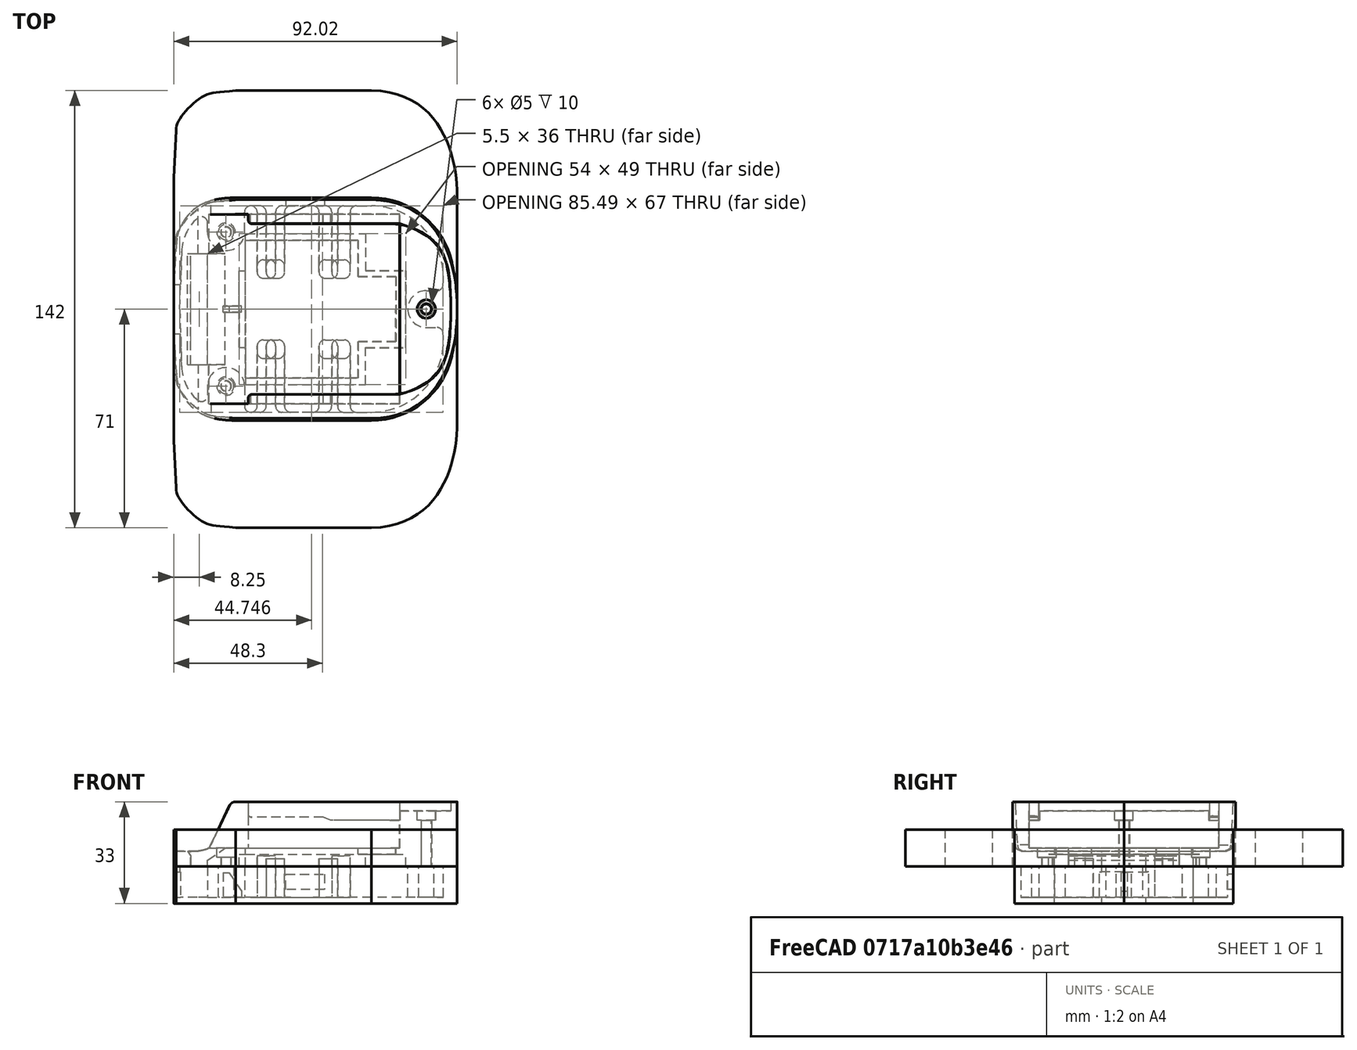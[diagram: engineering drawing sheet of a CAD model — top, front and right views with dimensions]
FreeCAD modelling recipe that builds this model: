
FCSTD DOCUMENT  (FreeCAD 1.0R39319 (Git))
Label: Makita LXT 18V - Battery Adapter v2
License: Creative Commons Attribution 4.0
LicenseURL: https://creativecommons.org/licenses/by/4.0/
objects: Sketcher::SketchObject×30, PartDesign::Pocket×23, TechDraw::DrawViewDimension×9, PartDesign::Pad×7, PartDesign::Body×5, TechDraw::DrawProjGroupItem×3, PartDesign::Mirrored×3, TechDraw::DrawSVGTemplate×2, TechDraw::DrawPage×2, Mesh::Feature×1, Part::Feature×1, TechDraw::DrawProjGroup×1
note: 180 computed .brp shape members not serialized (recipe doc carries the construction recipe); baked Part::Feature solids carry a one-line shape summary decoded from their .brp

FEATURE [Sketcher::SketchObject] Sketch
  ArcFitTolerance = 0
  AttachmentSupport = -> [XY_Plane]
  FullyConstrained = false
  MakeInternals = false
  MapMode = 5
  sketch-geometry (26):
    g0: ArcOfCircle CenterX=259.65 CenterY=-2.5774e-06 CenterZ=0 NormalX=0 NormalY=0 NormalZ=1 AngleXU=0 Radius=259.65 StartAngle=3.05831 EndAngle=3.14159
    g1: ArcOfCircle CenterX=16.3351 CenterY=20.3115 CenterZ=0 NormalX=0 NormalY=0 NormalZ=1 AngleXU=0 Radius=15.4888 StartAngle=1.76803 EndAngle=3.05831
    g2: LineSegment StartX=20 StartY=36.1629 StartZ=0 EndX=64.2 EndY=36.1629 EndZ=0
    g3: ArcOfCircle CenterX=64.2 CenterY=9.3939 CenterZ=0 NormalX=0 NormalY=0 NormalZ=1 AngleXU=0 Radius=26.769 StartAngle=0.218634 EndAngle=1.5708
    g4: ArcOfCircle CenterX=21.9206 CenterY=0 CenterZ=0 NormalX=0 NormalY=0 NormalZ=1 AngleXU=0 Radius=70.0794 StartAngle=0 EndAngle=0.218634
    g5: ArcOfCircle CenterX=20 CenterY=1.97116 CenterZ=0 NormalX=0 NormalY=0 NormalZ=1 AngleXU=0 Radius=34.1917 StartAngle=1.5708 EndAngle=1.76803
    g6: Circle CenterX=17 CenterY=25 CenterZ=0 NormalX=0 NormalY=0 NormalZ=1 AngleXU=0 Radius=1.6
    g7: ArcOfCircle CenterX=82 CenterY=0 CenterZ=0 NormalX=0 NormalY=0 NormalZ=1 AngleXU=0 Radius=1.6 StartAngle=0 EndAngle=3.14159
    g8: LineSegment StartX=23.3 StartY=0 StartZ=0 EndX=23.3 EndY=22.4 EndZ=0
    g9: LineSegment StartX=23.3 StartY=22.4 StartZ=0 EndX=59.9 EndY=22.4 EndZ=0
    g10: LineSegment StartX=59.9 StartY=22.4 StartZ=0 EndX=59.9 EndY=10.5 EndZ=0
    g11: LineSegment StartX=59.9 StartY=10.5 StartZ=0 EndX=72.1 EndY=10.5 EndZ=0
    g12: LineSegment StartX=72.1 StartY=10.5 StartZ=0 EndX=72.1 EndY=0 EndZ=0
    g13: ArcOfCircle CenterX=259.65 CenterY=2.5774e-06 CenterZ=0 NormalX=0 NormalY=0 NormalZ=1 AngleXU=0 Radius=259.65 StartAngle=3.14159 EndAngle=3.22488
    g14: ArcOfCircle CenterX=16.3351 CenterY=-20.3115 CenterZ=0 NormalX=0 NormalY=0 NormalZ=1 AngleXU=0 Radius=15.4888 StartAngle=3.22488 EndAngle=4.51516
    g15: LineSegment StartX=20 StartY=-36.1629 StartZ=0 EndX=64.2 EndY=-36.1629 EndZ=0
    g16: ArcOfCircle CenterX=64.2 CenterY=-9.3939 CenterZ=0 NormalX=0 NormalY=0 NormalZ=1 AngleXU=0 Radius=26.769 StartAngle=4.71239 EndAngle=6.06455
    g17: ArcOfCircle CenterX=21.9206 CenterY=0 CenterZ=0 NormalX=0 NormalY=0 NormalZ=1 AngleXU=0 Radius=70.0794 StartAngle=6.06455 EndAngle=6.28319
    g18: ArcOfCircle CenterX=20 CenterY=-1.97116 CenterZ=0 NormalX=0 NormalY=0 NormalZ=1 AngleXU=0 Radius=34.1917 StartAngle=4.51516 EndAngle=4.71239
    g19: Circle CenterX=17 CenterY=-25 CenterZ=0 NormalX=0 NormalY=0 NormalZ=1 AngleXU=0 Radius=1.6
    g20: ArcOfCircle CenterX=82 CenterY=0 CenterZ=0 NormalX=0 NormalY=0 NormalZ=1 AngleXU=0 Radius=1.6 StartAngle=3.14159 EndAngle=6.28319
    g21: LineSegment StartX=23.3 StartY=0 StartZ=0 EndX=23.3 EndY=-22.4 EndZ=0
    g22: LineSegment StartX=23.3 StartY=-22.4 StartZ=0 EndX=59.9 EndY=-22.4 EndZ=0
    g23: LineSegment StartX=59.9 StartY=-22.4 StartZ=0 EndX=59.9 EndY=-10.5 EndZ=0
    g24: LineSegment StartX=59.9 StartY=-10.5 StartZ=0 EndX=72.1 EndY=-10.5 EndZ=0
    g25: LineSegment StartX=72.1 StartY=-10.5 StartZ=0 EndX=72.1 EndY=0 EndZ=0
  constraints (64):
    c: Horizontal(g2)
    c: DistanceX(g2) = 20
    c: DistanceX(g2,g2) = 44.2
    c: Tangent(g4,g3) = -1.5708
    c: Tangent(g3,g2) = 1.5708
    c: Tangent(g1,g0) = -1.5708
    c: Tangent(g5,g2) = 1.5708
    c: Tangent(g5,g1) = -1.5708
    c: DistanceX(g0) = 0.9
    c: DistanceX(g1) = 13.3
    c: DistanceX(g4) = 92
    c: Coincident(g0,g-1)
    c: DistanceY(g0) = 21.6
    c: DistanceY(g1) = 35.5
    c: PointOnObject(g4,g-1)
    c: DistanceY(g3) = 15.2
    c: DistanceY(g6) = 25
    c: DistanceX(g6) = 17
    c: Diameter(g6) = 3.2
    c: PointOnObject(g7,g-1)
    c: PointOnObject(g7,g-1)
    c: PointOnObject(g7,g-1)
    c: DistanceX(g6,g7) = 65
    c: Equal(g7,g6)
    c: Tangent(g0,g-2)
    c: Perpendicular(g4,g-1)
    c: PointOnObject(g8,g-1)
    c: Vertical(g8)
    c: Coincident(g8,g9)
    c: Horizontal(g9)
    c: Coincident(g9,g10)
    c: Vertical(g10)
    c: Coincident(g10,g11)
    c: Horizontal(g11)
    c: Coincident(g11,g12)
    c: Vertical(g12)
    c: DistanceX(g8) = 23.3
    c: DistanceY(g8) = 22.4
    c: DistanceX(g9,g9) = 36.6
    c: DistanceY(g10,g10) = 11.9
    c: DistanceX(g11,g11) = 12.2
    c: PointOnObject(g12,g-1)
    c: Horizontal(g15)
    c: Tangent(g17,g16) = -1.5708
    c: Tangent(g16,g15) = -1.5708
    c: Tangent(g14,g13) = -1.5708
    c: Tangent(g18,g15) = -1.5708
    c: Tangent(g18,g14) = -1.5708
    c: Diameter(g19) = 3.2
    c: Equal(g20,g19)
    c: Vertical(g21)
    c: Coincident(g21,g22)
    c: Horizontal(g22)
    c: Coincident(g22,g23)
    c: Vertical(g23)
    c: Coincident(g23,g24)
    c: Horizontal(g24)
    c: Coincident(g24,g25)
    c: Vertical(g25)
    c: DistanceY(g15,g2) = 72.3257
    c: DistanceY(g19,g6) = 50
    c: DistanceX(g6,g7) = 66.6
    c: DistanceX(g6) = 17
    c: DistanceX(g4) = 92
FEATURE [Mesh::Feature] Makita_18V_Body  label="Makita 18V-Body"
  Placement = pos=(17,0,0) rot=(0,0,1;0rad)
FEATURE [PartDesign::Pad] Pad
  Direction = (0,0,1)
  Length = 21
  Length2 = 10
  Profile = -> Sketch
  ReferenceAxis = -> Sketch [N_Axis]
  Suppressed = false
  Type = 0
FEATURE [Sketcher::SketchObject] Sketch001
  ArcFitTolerance = 0
  AttachmentSupport = -> [XZ_Plane]
  FullyConstrained = true
  MakeInternals = false
  MapMode = 5
  Placement = pos=(0,0,0) rot=(1,0,0;1.5708rad)
  sketch-geometry (8):
    g0: LineSegment StartX=0 StartY=5 StartZ=0 EndX=0 EndY=21 EndZ=0
    g1: LineSegment StartX=0 StartY=21 StartZ=0 EndX=20 EndY=21 EndZ=0
    g2: LineSegment StartX=0 StartY=5 StartZ=0 EndX=7.9 EndY=5 EndZ=0
    g3: LineSegment StartX=18.2 StartY=19.8659 StartZ=0 EndX=11.9 EndY=6.7 EndZ=0
    g4: ArcOfCircle CenterX=20 CenterY=19.0045 CenterZ=0 NormalX=0 NormalY=0 NormalZ=1 AngleXU=0 Radius=1.99546 StartAngle=1.5708 EndAngle=2.69528
    g5: ArcOfCircle CenterX=10.0257 CenterY=7.59685 CenterZ=0 NormalX=0 NormalY=0 NormalZ=1 AngleXU=0 Radius=2.07779 StartAngle=4.99242 EndAngle=5.83688
    g6: ArcOfCircle CenterX=7.9 CenterY=5.60003 CenterZ=0 NormalX=0 NormalY=0 NormalZ=1 AngleXU=0 Radius=0.600034 StartAngle=4.71239 EndAngle=4.87983
    g7: ArcOfCircle CenterX=4.0509 CenterY=28.3729 CenterZ=0 NormalX=0 NormalY=0 NormalZ=1 AngleXU=0 Radius=23.6959 StartAngle=4.87983 EndAngle=4.99242
  constraints (22):
    c: PointOnObject(g0,g-2)
    c: PointOnObject(g0,g-2)
    c: Horizontal(g1)
    c: Coincident(g1,g0)
    c: DistanceY(g0) = 5
    c: DistanceY(g0) = 21
    c: Coincident(g2,g0)
    c: Horizontal(g2)
    c: Tangent(g4,g3) = -1.5708
    c: Tangent(g5,g3) = 1.5708
    c: Tangent(g4,g1) = 1.5708
    c: DistanceX(g1,g1) = 20
    c: DistanceX(g3) = 11.9
    c: DistanceY(g3) = 6.7
    c: DistanceX(g3) = 18.2
    c: Tangent(g6,g2) = -1.5708
    c: DistanceX(g2,g2) = 7.9
    c: Tangent(g7,g5) = -1.5708
    c: Tangent(g7,g6) = -1.5708
    c: DistanceX(g2,g6) = 0.1
    c: DistanceX(g5) = 10.6
    c: DistanceY(g5) = 5.6
FEATURE [PartDesign::Pocket] Pocket
  BaseFeature = -> Pad
  Direction = (0,1,-2e-16)
  Length = 5
  Length2 = 5
  Midplane = true
  Profile = -> Sketch001
  ReferenceAxis = -> Sketch001 [N_Axis]
  Suppressed = false
  Type = 1
FEATURE [Part::Feature] Makita_18V_Body001
  shape: bbox 92 x 71 x 21 mm, 5406 faces, 0 solids (baked)
FEATURE [Sketcher::SketchObject] Sketch002
  ArcFitTolerance = 0
  AttachmentSupport = -> [Pocket]
  FullyConstrained = false
  MakeInternals = false
  MapMode = 5
  Placement = pos=(0,0,21) rot=(0,0,1;0rad)
  sketch-geometry (16):
    g0: LineSegment StartX=24.2 StartY=30.78 StartZ=0 EndX=0 EndY=30.78 EndZ=0
    g1: LineSegment StartX=24.2 StartY=30.78 StartZ=0 EndX=24.2 EndY=28.88 EndZ=0
    g2: LineSegment StartX=25.4 StartY=27.68 StartZ=0 EndX=70.2 EndY=27.68 EndZ=0
    g3: ArcOfCircle CenterX=25.4 CenterY=28.88 CenterZ=0 NormalX=0 NormalY=0 NormalZ=1 AngleXU=0 Radius=1.2 StartAngle=3.14159 EndAngle=4.71239
    g4: ArcOfCircle CenterX=15.7361 CenterY=0 CenterZ=0 NormalX=0 NormalY=0 NormalZ=1 AngleXU=0 Radius=74.2639 StartAngle=0 EndAngle=0.199259
    g5: ArcOfCircle CenterX=74.666 CenterY=11.9002 CenterZ=0 NormalX=0 NormalY=0 NormalZ=1 AngleXU=0 Radius=14.1444 StartAngle=0.199259 EndAngle=0.868771
    g6: ArcOfCircle CenterX=70.2 CenterY=6.61972 CenterZ=0 NormalX=0 NormalY=0 NormalZ=1 AngleXU=0 Radius=21.0603 StartAngle=0.868771 EndAngle=1.5708
    g7: LineSegment StartX=0 StartY=0 StartZ=0 EndX=0 EndY=30.78 EndZ=0
    g8: LineSegment StartX=24.2 StartY=-30.78 StartZ=0 EndX=0 EndY=-30.78 EndZ=0
    g9: LineSegment StartX=24.2 StartY=-30.78 StartZ=0 EndX=24.2 EndY=-28.88 EndZ=0
    g10: LineSegment StartX=25.4 StartY=-27.68 StartZ=0 EndX=70.2 EndY=-27.68 EndZ=0
    g11: ArcOfCircle CenterX=25.4 CenterY=-28.88 CenterZ=0 NormalX=0 NormalY=0 NormalZ=1 AngleXU=0 Radius=1.2 StartAngle=1.5708 EndAngle=3.14159
    g12: ArcOfCircle CenterX=15.7361 CenterY=0 CenterZ=0 NormalX=0 NormalY=0 NormalZ=1 AngleXU=0 Radius=74.2639 StartAngle=6.08393 EndAngle=6.28319
    g13: ArcOfCircle CenterX=74.666 CenterY=-11.9002 CenterZ=0 NormalX=0 NormalY=0 NormalZ=1 AngleXU=0 Radius=14.1444 StartAngle=5.41441 EndAngle=6.08393
    g14: ArcOfCircle CenterX=70.2 CenterY=-6.61972 CenterZ=0 NormalX=0 NormalY=0 NormalZ=1 AngleXU=0 Radius=21.0603 StartAngle=4.71239 EndAngle=5.41441
    g15: LineSegment StartX=0 StartY=0 StartZ=0 EndX=0 EndY=-30.78 EndZ=0
  constraints (36):
    c: PointOnObject(g0,g-2)
    c: Horizontal(g0)
    c: DistanceY(g0) = 30.78
    c: DistanceX(g0,g0) = 24.2
    c: Coincident(g1,g0)
    c: Vertical(g1)
    c: Horizontal(g2)
    c: Tangent(g3,g1) = -1.5708
    c: Tangent(g3,g2) = -1.5708
    c: DistanceY(g1,g1) = 1.9
    c: Radius(g3) = 1.2
    c: PointOnObject(g4,g-1)
    c: Perpendicular(g4,g-1)
    c: DistanceX(g4) = 90
    c: DistanceY(g4) = 14.7
    c: Tangent(g6,g5) = -1.5708
    c: Tangent(g5,g4) = -1.5708
    c: Tangent(g6,g2) = 1.5708
    c: DistanceX(g2,g2) = 44.8
    c: DistanceX(g5) = 83.8
    c: DistanceY(g5) = 22.7
    c: PointOnObject(g7,g-1)
    c: Coincident(g7,g0)
    c: Vertical(g7)
    c: Horizontal(g8)
    c: Coincident(g9,g8)
    c: Vertical(g9)
    c: Horizontal(g10)
    c: Tangent(g11,g9) = 1.5708
    c: Tangent(g11,g10) = 1.5708
    c: Radius(g11) = 1.2
    c: Tangent(g14,g13) = -1.5708
    c: Tangent(g13,g12) = -1.5708
    c: Tangent(g14,g10) = -1.5708
    c: Coincident(g15,g8)
    c: Vertical(g15)
FEATURE [PartDesign::Pocket] Pocket001
  BaseFeature = -> Pocket
  Direction = (0,0,-1)
  Length = 3
  Length2 = 5
  Profile = -> Sketch002
  ReferenceAxis = -> Sketch002 [N_Axis]
  Suppressed = false
  Type = 0
FEATURE [Sketcher::SketchObject] Sketch003
  ArcFitTolerance = 0
  AttachmentSupport = -> [Pocket001]
  ExternalGeometry = -> [Sketch002]
  FullyConstrained = false
  MakeInternals = false
  MapMode = 5
  Placement = pos=(0,0,18) rot=(0,0,1;0rad)
  sketch-geometry (14):
    g0: LineSegment StartX=0 StartY=0 StartZ=0 EndX=0 EndY=30.78 EndZ=0
    g1: LineSegment StartX=0 StartY=30.78 StartZ=0 EndX=24.2 EndY=30.78 EndZ=0
    g2: LineSegment StartX=24.2 StartY=28.88 StartZ=0 EndX=24.2 EndY=30.78 EndZ=0
    g3: LineSegment StartX=25.4 StartY=27.68 StartZ=0 EndX=70.2 EndY=27.68 EndZ=0
    g4: ArcOfCircle CenterX=25.4 CenterY=28.88 CenterZ=0 NormalX=0 NormalY=0 NormalZ=1 AngleXU=0 Radius=1.2 StartAngle=3.14159 EndAngle=4.71239
    g5: LineSegment StartX=73.4 StartY=27.4355 StartZ=0 EndX=73.4 EndY=0 EndZ=0
    g6: ArcOfCircle CenterX=70.2 CenterY=6.61972 CenterZ=0 NormalX=0 NormalY=0 NormalZ=1 AngleXU=0 Radius=21.0603 StartAngle=1.41826 EndAngle=1.5708
    g7: LineSegment StartX=0 StartY=0 StartZ=0 EndX=0 EndY=-30.78 EndZ=0
    g8: LineSegment StartX=0 StartY=-30.78 StartZ=0 EndX=24.2 EndY=-30.78 EndZ=0
    g9: LineSegment StartX=24.2 StartY=-28.88 StartZ=0 EndX=24.2 EndY=-30.78 EndZ=0
    g10: LineSegment StartX=25.4 StartY=-27.68 StartZ=0 EndX=70.2 EndY=-27.68 EndZ=0
    g11: ArcOfCircle CenterX=25.4 CenterY=-28.88 CenterZ=0 NormalX=0 NormalY=0 NormalZ=1 AngleXU=0 Radius=1.2 StartAngle=1.5708 EndAngle=3.14159
    g12: LineSegment StartX=73.4 StartY=-27.4355 StartZ=0 EndX=73.4 EndY=0 EndZ=0
    g13: ArcOfCircle CenterX=70.2 CenterY=-6.61972 CenterZ=0 NormalX=0 NormalY=0 NormalZ=1 AngleXU=0 Radius=21.0603 StartAngle=4.71239 EndAngle=4.86492
  constraints (23):
    c: Coincident(g0,g-3)
    c: Coincident(g0,g-4)
    c: Coincident(g1,g0)
    c: Coincident(g1,g-4)
    c: Coincident(g2,g-7)
    c: Coincident(g2,g1)
    c: Coincident(g3,g-5)
    c: Coincident(g3,g-6)
    c: Coincident(g4,g2)
    c: Tangent(g4,g3) = -1.5708
    c: PointOnObject(g5,g-6)
    c: PointOnObject(g5,g-1)
    c: Vertical(g5)
    c: Coincident(g6,g5)
    c: Tangent(g6,g3) = 1.5708
    c: DistanceX(g5) = 73.4
    c: Coincident(g8,g7)
    c: Coincident(g9,g8)
    c: Coincident(g11,g9)
    c: Tangent(g11,g10) = 1.5708
    c: Vertical(g12)
    c: Coincident(g13,g12)
    c: Tangent(g13,g10) = -1.5708
FEATURE [PartDesign::Pocket] Pocket002
  BaseFeature = -> Pocket001
  Direction = (0,0,-1)
  Length = 12
  Length2 = 5
  Profile = -> Sketch003
  ReferenceAxis = -> Sketch003 [N_Axis]
  Suppressed = false
  Type = 0
FEATURE [Sketcher::SketchObject] Sketch004
  ArcFitTolerance = 0
  AttachmentSupport = -> [Pocket002]
  ExternalGeometry = -> [Pocket002]
  FullyConstrained = true
  MakeInternals = false
  MapMode = 5
  Placement = pos=(0,0,6) rot=(0,0,1;0rad)
  sketch-geometry (2):
    g0: Circle CenterX=17 CenterY=25 CenterZ=0 NormalX=0 NormalY=0 NormalZ=1 AngleXU=0 Radius=3
    g1: Circle CenterX=17 CenterY=-25 CenterZ=0 NormalX=0 NormalY=0 NormalZ=1 AngleXU=0 Radius=3
  constraints (4):
    c: Symmetric(g1,g0,g-1)
    c: Equal(g0,g1)
    c: Coincident(g-3,g0)
    c: Diameter(g0) = 6
FEATURE [PartDesign::Pocket] Pocket003
  BaseFeature = -> Pocket002
  Direction = (0,0,-1)
  Length = 3
  Length2 = 5
  Profile = -> Sketch004
  ReferenceAxis = -> Sketch004 [N_Axis]
  Suppressed = false
  Type = 0
FEATURE [Sketcher::SketchObject] Sketch005
  ArcFitTolerance = 0
  AttachmentSupport = -> [Pocket003]
  ExternalGeometry = -> [Pocket003]
  FullyConstrained = true
  MakeInternals = false
  MapMode = 5
  Placement = pos=(0,0,18) rot=(0,0,1;0rad)
  sketch-geometry (1):
    g0: Circle CenterX=82 CenterY=0 CenterZ=0 NormalX=0 NormalY=0 NormalZ=1 AngleXU=0 Radius=3
  constraints (2):
    c: Coincident(g0,g-3)
    c: Diameter(g0) = 6
FEATURE [PartDesign::Pocket] Pocket004
  BaseFeature = -> Pocket003
  Direction = (0,0,-1)
  Length = 3
  Length2 = 5
  Profile = -> Sketch005
  ReferenceAxis = -> Sketch005 [N_Axis]
  Suppressed = false
  Type = 0
FEATURE [Sketcher::SketchObject] Sketch006
  ArcFitTolerance = 0
  AttachmentSupport = -> [XZ_Plane]
  ExternalGeometry = -> [Sketch003]
  FullyConstrained = true
  MakeInternals = false
  MapMode = 5
  Placement = pos=(0,0,0) rot=(1,0,0;1.5708rad)
  sketch-geometry (7):
    g0: LineSegment StartX=73.4 StartY=15 StartZ=0 EndX=51 EndY=15 EndZ=0
    g1: LineSegment StartX=51 StartY=15 StartZ=0 EndX=48.5 EndY=16 EndZ=0
    g2: LineSegment StartX=48.5 StartY=16 StartZ=0 EndX=25 EndY=16 EndZ=0
    g3: LineSegment StartX=24.2 StartY=16.4 StartZ=0 EndX=25 EndY=16 EndZ=0
    g4: LineSegment StartX=24.2 StartY=16.4 StartZ=0 EndX=24.2 EndY=6 EndZ=0
    g5: LineSegment StartX=24.2 StartY=6 StartZ=0 EndX=73.4 EndY=6 EndZ=0
    g6: LineSegment StartX=73.4 StartY=6 StartZ=0 EndX=73.4 EndY=15 EndZ=0
  constraints (21):
    c: Horizontal(g0)
    c: Coincident(g1,g0)
    c: Coincident(g2,g1)
    c: Horizontal(g2)
    c: Coincident(g2,g3)
    c: Coincident(g4,g3)
    c: Vertical(g4)
    c: Coincident(g5,g4)
    c: Horizontal(g5)
    c: Coincident(g6,g5)
    c: Coincident(g6,g0)
    c: Vertical(g6)
    c: Vertical(g0,g-3)
    c: Vertical(g3,g-5)
    c: DistanceY(g4) = 6
    c: DistanceY(g4,g4) = 10.4
    c: DistanceY(g2) = 16
    c: DistanceX(g3,g2) = 0.8
    c: DistanceX(g2,g2) = 23.5
    c: DistanceY(g0) = 15
    c: DistanceX(g1,g0) = 2.5
FEATURE [PartDesign::Pocket] Pocket005
  BaseFeature = -> Pocket004
  Direction = (0,1,-2e-16)
  Length = 61.6
  Length2 = 5
  Midplane = true
  Profile = -> Sketch006
  ReferenceAxis = -> Sketch006 [N_Axis]
  Suppressed = false
  Type = 0
FEATURE [Sketcher::SketchObject] Sketch007
  ArcFitTolerance = 0
  AttachmentSupport = -> [Pocket005]
  ExternalGeometry = -> [Pocket005]
  FullyConstrained = false
  MakeInternals = false
  MapMode = 5
  Placement = pos=(0,0,0) rot=(1,0,0;3.14159rad)
  sketch-geometry (14):
    g0: LineSegment StartX=21.3 StartY=0 StartZ=0 EndX=21.3 EndY=12.5 EndZ=0
    g1: LineSegment StartX=21.3 StartY=12.5 StartZ=0 EndX=23.3 EndY=12.5 EndZ=0
    g2: LineSegment StartX=23.3 StartY=12.5 StartZ=0 EndX=23.3 EndY=24.5 EndZ=0
    g3: LineSegment StartX=23.3 StartY=24.5 StartZ=0 EndX=62.3 EndY=24.5 EndZ=0
    g4: LineSegment StartX=62.3 StartY=24.5 StartZ=0 EndX=62.3 EndY=12.5 EndZ=0
    g5: LineSegment StartX=62.3 StartY=12.5 StartZ=0 EndX=75.3 EndY=12.5 EndZ=0
    g6: LineSegment StartX=75.3 StartY=12.5 StartZ=0 EndX=75.3 EndY=0 EndZ=0
    g7: LineSegment StartX=21.3 StartY=0 StartZ=0 EndX=21.3 EndY=-12.5 EndZ=0
    g8: LineSegment StartX=21.3 StartY=-12.5 StartZ=0 EndX=23.3 EndY=-12.5 EndZ=0
    g9: LineSegment StartX=23.3 StartY=-12.5 StartZ=0 EndX=23.3 EndY=-24.5 EndZ=0
    g10: LineSegment StartX=23.3 StartY=-24.5 StartZ=0 EndX=62.3 EndY=-24.5 EndZ=0
    g11: LineSegment StartX=62.3 StartY=-24.5 StartZ=0 EndX=62.3 EndY=-12.5 EndZ=0
    g12: LineSegment StartX=62.3 StartY=-12.5 StartZ=0 EndX=75.3 EndY=-12.5 EndZ=0
    g13: LineSegment StartX=75.3 StartY=-12.5 StartZ=0 EndX=75.3 EndY=0 EndZ=0
  constraints (35):
    c: PointOnObject(g0,g-1)
    c: Vertical(g0)
    c: Coincident(g0,g1)
    c: PointOnObject(g1,g-3)
    c: Horizontal(g1)
    c: Coincident(g1,g2)
    c: Vertical(g2)
    c: Coincident(g2,g3)
    c: Horizontal(g3)
    c: Coincident(g3,g4)
    c: Vertical(g4)
    c: Coincident(g4,g5)
    c: Horizontal(g5)
    c: Coincident(g5,g6)
    c: PointOnObject(g6,g-1)
    c: Vertical(g6)
    c: DistanceY(g2) = 24.5
    c: DistanceY(g0,g0) = 12.5
    c: DistanceX(g1,g1) = 2
    c: DistanceX(g-4,g3) = 2.4
    c: DistanceY(g-5,g4) = 2
    c: DistanceX(g-5,g5) = 3.2
    c: Vertical(g7)
    c: Coincident(g7,g8)
    c: Horizontal(g8)
    c: Coincident(g8,g9)
    c: Vertical(g9)
    c: Coincident(g9,g10)
    c: Horizontal(g10)
    c: Coincident(g10,g11)
    c: Vertical(g11)
    c: Coincident(g11,g12)
    c: Horizontal(g12)
    c: Coincident(g12,g13)
    c: Vertical(g13)
FEATURE [PartDesign::Pocket] Pocket006
  BaseFeature = -> Pocket005
  Direction = (0,0,1)
  Length = 4
  Length2 = 5
  Profile = -> Sketch007
  ReferenceAxis = -> Sketch007 [N_Axis]
  Suppressed = false
  Type = 0
FEATURE [Sketcher::SketchObject] Sketch008
  ArcFitTolerance = 0
  AttachmentSupport = -> [XZ_Plane]
  FullyConstrained = true
  MakeInternals = false
  MapMode = 5
  Placement = pos=(0,0,0) rot=(1,0,0;1.5708rad)
  sketch-geometry (7):
    g0: LineSegment StartX=5.5 StartY=0 StartZ=0 EndX=11 EndY=0 EndZ=0
    g1: LineSegment StartX=11 StartY=0 StartZ=0 EndX=11 EndY=2 EndZ=0
    g2: LineSegment StartX=11 StartY=2 StartZ=0 EndX=16.7 EndY=6 EndZ=0
    g3: LineSegment StartX=16.7 StartY=6 StartZ=0 EndX=4.45 EndY=6 EndZ=0
    g4: LineSegment StartX=4.45 StartY=6 StartZ=0 EndX=4.45 EndY=5 EndZ=0
    g5: LineSegment StartX=4.45 StartY=5 StartZ=0 EndX=5.5 EndY=3.5 EndZ=0
    g6: LineSegment StartX=5.5 StartY=3.5 StartZ=0 EndX=5.5 EndY=0 EndZ=0
  constraints (21):
    c: PointOnObject(g0,g-1)
    c: PointOnObject(g0,g-1)
    c: Coincident(g0,g1)
    c: Vertical(g1)
    c: Coincident(g1,g2)
    c: Coincident(g2,g3)
    c: Horizontal(g3)
    c: Coincident(g3,g4)
    c: Vertical(g4)
    c: Coincident(g4,g5)
    c: Coincident(g5,g6)
    c: Coincident(g6,g0)
    c: Vertical(g6)
    c: DistanceX(g0) = 5.5
    c: DistanceX(g0) = 11
    c: DistanceY(g6,g6) = 3.5
    c: DistanceY(g1,g1) = 2
    c: DistanceY(g2) = 6
    c: DistanceX(g2) = 16.7
    c: DistanceY(g4) = 5
    c: DistanceX(g4) = 4.45
FEATURE [PartDesign::Pocket] Pocket007
  BaseFeature = -> Pocket006
  Direction = (0,1,-2e-16)
  Length = 36
  Length2 = 5
  Midplane = true
  Profile = -> Sketch008
  ReferenceAxis = -> Sketch008 [N_Axis]
  Suppressed = false
  Type = 0
FEATURE [PartDesign::Body] Body  label="Battery mount"
  AllowCompound = false
  Group = -> [Sketch,Pad,Sketch001,Pocket,Sketch002,Pocket001,Sketch003,Pocket002,Sketch004,Pocket003,Sketch005,Pocket004,Sketch006,Pocket005,Sketch007,Pocket006,Sketch008,Pocket007]
  Origin = -> Origin
  Tip = -> Pocket007
FEATURE [TechDraw::DrawSVGTemplate] Template
  EditableTexts = approval_person=B. Hecate; creator=Jon Sagebrand; date_of_issue=2026-02-17; document_type=Component Drawing; general_tolerances=ISO 2768-m; identification_number=DN; language_code=EN; legal_owner_1=Jonix; part_material=Stainless steel Mat.No. 1.4301; revision_index=AAA; scale=1 : 1; sheet_number=1 / 1; title=Makita LXT  - 18V - Battery holder
  Height = 210
  Orientation = 1
  Template = <path>
  Width = 297
FEATURE [TechDraw::DrawProjGroupItem] View
  CoarseView = false
  Direction = (0,0,-1)
  Focus = 100
  HardHidden = false
  IsoCount = 0
  IsoHidden = false
  IsoVisible = false
  LockPosition = false
  Perspective = false
  Rotation = 0
  RotationVector = (1,0,0)
  ScaleType = 0
  ScrubCount = 1
  SeamHidden = false
  SeamVisible = false
  SmoothHidden = false
  SmoothVisible = true
  Source = -> [Pocket007]
  Type = 0
  X = 157.417
  XDirection = (1,0,0)
  Y = 121.596
FEATURE [TechDraw::DrawViewDimension] Dimension
  AngleOverride = false
  Arbitrary = false
  ArbitraryTolerances = false
  BoxCorners = (2) [(-46,-36.1629,0),(46,36.1629,0)]
  EqualTolerance = true
  ExtensionAngle = 0
  FormatSpec = %.2w
  FormatSpecOverTolerance = %+.2w
  FormatSpecUnderTolerance = %+.2w
  Inverted = false
  LineAngle = 0
  LockPosition = false
  MeasureType = 1
  OverTolerance = 0
  References2D = -> [View]
  Rotation = 0
  ScaleType = 0
  TheoreticalExact = false
  Type = 2
  UnderTolerance = 0
  X = -60.9397
  Y = 3.59505
FEATURE [TechDraw::DrawViewDimension] Dimension001
  AngleOverride = false
  Arbitrary = false
  ArbitraryTolerances = false
  BoxCorners = (2) [(-46,-36.1629,0),(46,36.1629,0)]
  EqualTolerance = true
  ExtensionAngle = 0
  FormatSpec = %.2w
  FormatSpecOverTolerance = %+.2w
  FormatSpecUnderTolerance = %+.2w
  Inverted = false
  LineAngle = 0
  LockPosition = false
  MeasureType = 1
  OverTolerance = 0
  References2D = -> [View]
  Rotation = 0
  ScaleType = 0
  TheoreticalExact = false
  Type = 2
  UnderTolerance = 0
  X = -74.0234
  Y = 0
FEATURE [TechDraw::DrawViewDimension] Dimension002
  AngleOverride = false
  Arbitrary = false
  ArbitraryTolerances = false
  BoxCorners = (2) [(-46,-36.1629,0),(46,36.1629,0)]
  EqualTolerance = true
  ExtensionAngle = 0
  FormatSpec = %.2w
  FormatSpecOverTolerance = %+.2w
  FormatSpecUnderTolerance = %+.2w
  Inverted = false
  LineAngle = 0
  LockPosition = false
  MeasureType = 1
  OverTolerance = 0
  References2D = -> [View]
  Rotation = 0
  ScaleType = 0
  TheoreticalExact = false
  Type = 1
  UnderTolerance = 0
  X = 3.5
  Y = 57.7106
FEATURE [TechDraw::DrawViewDimension] Dimension003
  AngleOverride = false
  Arbitrary = false
  ArbitraryTolerances = false
  BoxCorners = (2) [(-46,-36.1629,0),(46,36.1629,0)]
  EqualTolerance = true
  ExtensionAngle = 0
  FormatSpec = %.2w
  FormatSpecOverTolerance = %+.2w
  FormatSpecUnderTolerance = %+.2w
  Inverted = false
  LineAngle = 0
  LockPosition = false
  MeasureType = 1
  OverTolerance = 0
  References2D = -> [View]
  Rotation = 0
  ScaleType = 0
  TheoreticalExact = false
  Type = 1
  UnderTolerance = 0
  X = 0
  Y = -48.6903
FEATURE [TechDraw::DrawViewDimension] Dimension004
  AngleOverride = false
  Arbitrary = false
  ArbitraryTolerances = false
  BoxCorners = (2) [(-46,-36.1629,0),(46,36.1629,0)]
  EqualTolerance = true
  ExtensionAngle = 0
  FormatSpec = %.2w
  FormatSpecOverTolerance = %+.2w
  FormatSpecUnderTolerance = %+.2w
  Inverted = false
  LineAngle = 0
  LockPosition = false
  MeasureType = 1
  OverTolerance = 0
  References2D = -> [View]
  Rotation = 0
  ScaleType = 0
  TheoreticalExact = false
  Type = 1
  UnderTolerance = 0
  X = -37.5
  Y = 57.7106
FEATURE [TechDraw::DrawViewDimension] Dimension005
  AngleOverride = false
  Arbitrary = false
  ArbitraryTolerances = false
  BoxCorners = (2) [(-46,-36.1629,0),(46,36.1629,0)]
  EqualTolerance = true
  ExtensionAngle = 0
  FormatSpec = %.2w
  FormatSpecOverTolerance = %+.2w
  FormatSpecUnderTolerance = %+.2w
  Inverted = false
  LineAngle = 0
  LockPosition = false
  MeasureType = 1
  OverTolerance = 0
  References2D = -> [View]
  Rotation = 0
  ScaleType = 0
  TheoreticalExact = false
  Type = 1
  UnderTolerance = 0
  X = 41
  Y = 57.7106
FEATURE [TechDraw::DrawPage] Page
  KeepUpdated = true
  NextBalloonIndex = 1
  ProjectionType = 0
  Template = -> Template
  Views = -> [View,Dimension,Dimension001,Dimension002,Dimension003,Dimension004,Dimension005]
FEATURE [Sketcher::SketchObject] Sketch009
  ArcFitTolerance = 1e-06
  AttachmentSupport = -> [XY_Plane001]
  FullyConstrained = false
  MakeInternals = false
  MapMode = 5
  sketch-geometry (35):
    g0: LineSegment StartX=23.3 StartY=22.3 StartZ=0 EndX=59.9 EndY=22.3 EndZ=0
    g1: LineSegment StartX=59.9 StartY=22.3 StartZ=0 EndX=59.9 EndY=10.55 EndZ=0
    g2: LineSegment StartX=59.9 StartY=10.55 StartZ=0 EndX=72.15 EndY=10.55 EndZ=0
    g3: LineSegment StartX=72.15 StartY=10.55 StartZ=0 EndX=72.15 EndY=0 EndZ=0
    g4: LineSegment StartX=72.15 StartY=0 StartZ=0 EndX=80.25 EndY=2e-16 EndZ=0
    g5: LineSegment StartX=83.75 StartY=0 StartZ=0 EndX=92 EndY=0 EndZ=0
    g6: ArcOfCircle CenterX=82 CenterY=0 CenterZ=0 NormalX=0 NormalY=0 NormalZ=1 AngleXU=0 Radius=1.75 StartAngle=0 EndAngle=3.14159
    g7: LineSegment StartX=0 StartY=6.35e-14 StartZ=0 EndX=5.5 EndY=0 EndZ=0
    g8: LineSegment StartX=5.5 StartY=0 StartZ=0 EndX=5.5 EndY=18 EndZ=0
    g9: LineSegment StartX=5.5 StartY=18 StartZ=0 EndX=11 EndY=18 EndZ=0
    g10: LineSegment StartX=11 StartY=0 StartZ=0 EndX=23.3 EndY=0 EndZ=0
    g11: LineSegment StartX=0.05 StartY=7.2 StartZ=0 EndX=0.75 EndY=22.55 EndZ=0
    g12: ArcOfCircle CenterX=518.425 CenterY=0 CenterZ=0 NormalX=0 NormalY=0 NormalZ=1 AngleXU=0 Radius=518.425 StartAngle=3.1277 EndAngle=3.14159
    g13: LineSegment StartX=11 StartY=0 StartZ=0 EndX=11 EndY=18 EndZ=0
    g14: LineSegment StartX=20.1 StartY=35.5 StartZ=0 EndX=64.2 EndY=35.5 EndZ=0
    g15-g20: Circle [constr] x6 (B-spline internal-alignment scaffolding for g21; pole/knot coordinates omitted)
    g21: BSplineCurve PolesCount=6 KnotsCount=4 Degree=3 IsPeriodic=0
    g22-g25: GeomPoint [constr] x4 (B-spline internal-alignment scaffolding for g21; pole/knot coordinates omitted)
    g26-g29: Circle [constr] x4 (B-spline internal-alignment scaffolding for g30; pole/knot coordinates omitted)
    g30: BSplineCurve PolesCount=4 KnotsCount=2 Degree=3 IsPeriodic=0
    g31: GeomPoint [constr] X=92 Y=0 Z=0
    g32: GeomPoint [constr] X=64.2 Y=35.5 Z=0
    g33: Circle CenterX=17 CenterY=25 CenterZ=0 NormalX=0 NormalY=0 NormalZ=1 AngleXU=0 Radius=1.75
    g34: LineSegment StartX=23.3 StartY=0 StartZ=0 EndX=23.3 EndY=22.3 EndZ=0
  constraints (71):
    c: PointOnObject(g10,g-1)
    c: Horizontal(g0)
    c: Coincident(g0,g1)
    c: Vertical(g1)
    c: Coincident(g1,g2)
    c: Horizontal(g2)
    c: Coincident(g2,g3)
    c: PointOnObject(g3,g-1)
    c: Vertical(g3)
    c: Coincident(g4,g3)
    c: PointOnObject(g4,g-1)
    c: PointOnObject(g5,g-1)
    c: PointOnObject(g5,g-1)
    c: Coincident(g6,g4)
    c: Coincident(g6,g5)
    c: PointOnObject(g6,g-1)
    c: Coincident(g7,g-1)
    c: PointOnObject(g7,g-1)
    c: Coincident(g8,g7)
    c: Vertical(g8)
    c: Horizontal(g9)
    c: PointOnObject(g10,g-1)
    c: DistanceX(g7,g7) = 5.5
    c: DistanceX(g7,g10) = 5.5
    c: Coincident(g9,g8)
    c: DistanceY(g8,g8) = 18
    c: Diameter(g6) = 3.5
    c: DistanceX(g5,g5) = 8.25
    c: DistanceX(g5) = 92
    c: DistanceX(g11) = 0.75
    c: DistanceY(g11) = 22.55
    c: Coincident(g12,g7)
    c: Coincident(g12,g11)
    c: DistanceX(g11) = 0.05
    c: DistanceY(g11) = 7.2
    c: Perpendicular(g12,g-1)
    c: Radius(g12) = 518.425
    c: Coincident(g13,g10)
    c: Coincident(g13,g9)
    c: Vertical(g13)
    c: Horizontal(g14)
    c: DistanceY(g14) = 35.5
    c: DistanceX(g14) = 20.1
    c: DistanceX(g14,g14) = 44.1
    c: Weight(g15) = 1
    c: Equal(g15, g16-g20) x5
    c: InternalAlignment(g15-g20 -> g21) x6
    c: InternalAlignment(g22-g25 -> g21) x4
    c: Coincident(g15,g11)
    c: Coincident(g20,g14)
    c: Weight(g26) = 1
    c: Equal(g26,g27)
    c: Equal(g26,g28)
    c: Equal(g26,g29)
    c: InternalAlignment(g26-g29 -> g30) x4
    c: InternalAlignment(g31,g30)
    c: InternalAlignment(g32,g30)
    c: Coincident(g26,g5)
    c: Coincident(g29,g14)
    c: DistanceY(g33) = 25
    c: DistanceX(g33,g6) = 65
    c: Equal(g33,g6)
    c: Coincident(g34,g10)
    c: Coincident(g34,g0)
    c: Vertical(g34)
    c: DistanceX(g10,g10) = 12.3
    c: DistanceY(g34,g34) = 22.3
    c: DistanceX(g0,g0) = 36.6
    c: DistanceY(g1,g1) = 11.75
    c: DistanceX(g2,g2) = 12.25
    c: DistanceX(g4,g4) = 8.1
FEATURE [PartDesign::Pad] Pad001
  Direction = (0,0,1)
  Length = 21
  Length2 = 10
  Profile = -> Sketch009
  ReferenceAxis = -> Sketch009 [N_Axis]
  Refine = true
  Suppressed = false
  Type = 0
FEATURE [Sketcher::SketchObject] Sketch010
  ArcFitTolerance = 1e-06
  AttachmentSupport = -> [Pad001]
  ExternalGeometry = -> [Pad001]
  FullyConstrained = false
  MakeInternals = false
  MapMode = 5
  Placement = pos=(0,0,0) rot=(1,0,0;1.5708rad)
  sketch-geometry (14):
    g0: LineSegment StartX=7.9 StartY=5 StartZ=0 EndX=0 EndY=5 EndZ=0
    g1: LineSegment StartX=0 StartY=5 StartZ=0 EndX=0 EndY=21 EndZ=0
    g2: LineSegment StartX=0 StartY=21 StartZ=0 EndX=20.05 EndY=21 EndZ=0
    g3: LineSegment StartX=18.1059 StartY=19.7681 StartZ=0 EndX=12.1 EndY=7.05 EndZ=0
    g4: ArcOfCircle CenterX=20.05 CenterY=18.85 CenterZ=0 NormalX=0 NormalY=0 NormalZ=1 AngleXU=0 Radius=2.15 StartAngle=1.5708 EndAngle=2.70041
    g5-g9: Circle [constr] x5 (B-spline internal-alignment scaffolding for g10; pole/knot coordinates omitted)
    g10: BSplineCurve PolesCount=5 KnotsCount=3 Degree=3 IsPeriodic=0
    g11: GeomPoint [constr] X=12.1 Y=7.05 Z=0
    g12: GeomPoint [constr] X=11.1765 Y=5.88818 Z=0
    g13: GeomPoint [constr] X=7.9 Y=5 Z=0
  constraints (23):
    c: PointOnObject(g0,g-2)
    c: Horizontal(g0)
    c: Coincident(g0,g1)
    c: Coincident(g1,g-3)
    c: Coincident(g1,g2)
    c: Horizontal(g2)
    c: DistanceY(g0) = 5
    c: DistanceX(g0,g0) = 7.9
    c: DistanceX(g2,g2) = 20.05
    c: DistanceX(g3) = 12.1
    c: DistanceY(g0,g3) = 2.05
    c: Coincident(g4,g3)
    c: Tangent(g4,g2) = 1.5708
    c: Tangent(g3,g4,g3) = -1.5708
    c: Radius(g4) = 2.15
    c: Weight(g5) = 1
    c: Equal(g5, g6-g9) x4
    c: InternalAlignment(g5-g9 -> g10) x5
    c: InternalAlignment(g11,g10)
    c: InternalAlignment(g12,g10)
    c: InternalAlignment(g13,g10)
    c: Coincident(g5,g3)
    c: Coincident(g9,g0)
FEATURE [PartDesign::Pocket] Pocket008
  BaseFeature = -> Pad001
  Direction = (0,1,-2e-16)
  Length = 5
  Length2 = 5
  Profile = -> Sketch010
  ReferenceAxis = -> Sketch010 [N_Axis]
  Refine = true
  Suppressed = false
  Type = 1
FEATURE [Sketcher::SketchObject] Sketch011
  ArcFitTolerance = 1e-06
  AttachmentSupport = -> [Pocket008]
  ExternalGeometry = -> [Pocket008]
  FullyConstrained = true
  MakeInternals = false
  MapMode = 5
  Placement = pos=(0,0,21) rot=(0,0,1;0rad)
  sketch-geometry (13):
    g0: LineSegment StartX=11 StartY=30.8 StartZ=0 EndX=11 EndY=0 EndZ=0
    g1: LineSegment StartX=11 StartY=0 StartZ=0 EndX=23.3 EndY=0 EndZ=0
    g2: LineSegment StartX=23.3 StartY=0 StartZ=0 EndX=23.3 EndY=22.3 EndZ=0
    g3: LineSegment StartX=23.3 StartY=22.3 StartZ=0 EndX=59.9 EndY=22.3 EndZ=0
    g4: LineSegment StartX=59.9 StartY=22.3 StartZ=0 EndX=59.9 EndY=10.55 EndZ=0
    g5: LineSegment StartX=59.9 StartY=10.55 StartZ=0 EndX=72.15 EndY=10.55 EndZ=0
    g6: LineSegment StartX=72.15 StartY=10.55 StartZ=0 EndX=72.15 EndY=0 EndZ=0
    g7: LineSegment StartX=72.15 StartY=0 StartZ=0 EndX=73.35 EndY=0 EndZ=0
    g8: LineSegment StartX=73.35 StartY=27.75 StartZ=0 EndX=25.4 EndY=27.75 EndZ=0
    g9: LineSegment StartX=24.2 StartY=28.95 StartZ=0 EndX=24.2 EndY=30.8 EndZ=0
    g10: LineSegment StartX=24.2 StartY=30.8 StartZ=0 EndX=11 EndY=30.8 EndZ=0
    g11: ArcOfCircle CenterX=25.4 CenterY=28.95 CenterZ=0 NormalX=0 NormalY=0 NormalZ=1 AngleXU=0 Radius=1.2 StartAngle=3.14159 EndAngle=4.71239
    g12: LineSegment StartX=73.35 StartY=27.75 StartZ=0 EndX=73.35 EndY=0 EndZ=0
  constraints (33):
    c: Vertical(g0)
    c: Coincident(g0,g1)
    c: PointOnObject(g1,g-1)
    c: Coincident(g1,g2)
    c: Coincident(g2,g-4)
    c: Vertical(g2)
    c: Coincident(g2,g3)
    c: Coincident(g3,g-4)
    c: Coincident(g3,g4)
    c: Coincident(g4,g-3)
    c: Coincident(g4,g5)
    c: Coincident(g5,g-3)
    c: Coincident(g5,g6)
    c: PointOnObject(g6,g-1)
    c: Vertical(g6)
    c: Coincident(g6,g7)
    c: PointOnObject(g7,g-1)
    c: Horizontal(g8)
    c: Vertical(g9)
    c: Coincident(g9,g10)
    c: Coincident(g10,g0)
    c: Horizontal(g10)
    c: Tangent(g11,g8) = 1.5708
    c: Tangent(g11,g9) = 1.5708
    c: DistanceY(g0) = 30.8
    c: DistanceX(g9) = 24.2
    c: DistanceY(g8) = 27.75
    c: Radius(g11) = 1.2
    c: DistanceX(g8,g8) = 47.95
    c: Coincident(g12,g8)
    c: Coincident(g12,g7)
    c: Vertical(g12)
    c: Coincident(g0,g-5)
FEATURE [PartDesign::Pocket] Pocket009
  BaseFeature = -> Pocket008
  Direction = (0,0,-1)
  Length = 15
  Length2 = 5
  Profile = -> Sketch011
  ReferenceAxis = -> Sketch011 [N_Axis]
  Refine = true
  Suppressed = false
  Type = 0
FEATURE [Sketcher::SketchObject] Sketch012
  ArcFitTolerance = 1e-06
  AttachmentSupport = -> [Pocket009]
  ExternalGeometry = -> [Pocket009]
  FullyConstrained = true
  MakeInternals = false
  MapMode = 5
  Placement = pos=(0,0,0) rot=(1,0,0;1.5708rad)
  sketch-geometry (3):
    g0: LineSegment StartX=16.7 StartY=6 StartZ=0 EndX=11 EndY=6 EndZ=0
    g1: LineSegment StartX=11 StartY=6 StartZ=0 EndX=11 EndY=2 EndZ=0
    g2: LineSegment StartX=11 StartY=2 StartZ=0 EndX=16.7 EndY=6 EndZ=0
  constraints (9):
    c: PointOnObject(g0,g-3)
    c: Horizontal(g0)
    c: Coincident(g0,g1)
    c: PointOnObject(g1,g-4)
    c: Coincident(g1,g2)
    c: Coincident(g2,g0)
    c: Vertical(g1)
    c: DistanceX(g0,g0) = 5.7
    c: DistanceY(g1,g1) = 4
FEATURE [PartDesign::Pocket] Pocket010
  BaseFeature = -> Pocket009
  Direction = (0,1,-2e-16)
  Length = 0
  Length2 = 5
  Profile = -> Sketch012
  ReferenceAxis = -> Sketch012 [N_Axis]
  Refine = true
  Suppressed = false
  Type = 3
  UpToFace = -> Pocket009 [Face21]
FEATURE [Sketcher::SketchObject] Sketch013
  ArcFitTolerance = 1e-06
  AttachmentSupport = -> [Pocket010]
  ExternalGeometry = -> [Pocket010]
  FullyConstrained = true
  MakeInternals = false
  MapMode = 5
  Placement = pos=(0,0,0) rot=(1,0,0;3.14159rad)
  sketch-geometry (14):
    g0: LineSegment StartX=72.15 StartY=-10.55 StartZ=0 EndX=59.9 EndY=-10.55 EndZ=0
    g1: LineSegment StartX=59.9 StartY=-10.55 StartZ=0 EndX=59.9 EndY=-22.3 EndZ=0
    g2: LineSegment StartX=59.9 StartY=-22.3 StartZ=0 EndX=23.3 EndY=-22.3 EndZ=0
    g3: LineSegment StartX=23.3 StartY=-22.3 StartZ=0 EndX=23.3 EndY=-24.5 EndZ=0
    g4: LineSegment StartX=23.3 StartY=-24.5 StartZ=0 EndX=62.3 EndY=-24.5 EndZ=0
    g5: LineSegment StartX=62.3 StartY=-24.5 StartZ=0 EndX=62.3 EndY=-12.55 EndZ=0
    g6: LineSegment StartX=62.3 StartY=-12.55 StartZ=0 EndX=75.35 EndY=-12.55 EndZ=0
    g7: LineSegment StartX=75.35 StartY=-12.55 StartZ=0 EndX=75.35 EndY=0 EndZ=0
    g8: LineSegment StartX=75.35 StartY=0 StartZ=0 EndX=72.15 EndY=0 EndZ=0
    g9: LineSegment StartX=72.15 StartY=0 StartZ=0 EndX=72.15 EndY=-10.55 EndZ=0
    g10: LineSegment StartX=23.3 StartY=0 StartZ=0 EndX=21.3 EndY=0 EndZ=0
    g11: LineSegment StartX=21.3 StartY=0 StartZ=0 EndX=21.3 EndY=-12.5 EndZ=0
    g12: LineSegment StartX=21.3 StartY=-12.5 StartZ=0 EndX=23.3 EndY=-12.5 EndZ=0
    g13: LineSegment StartX=23.3 StartY=-12.5 StartZ=0 EndX=23.3 EndY=0 EndZ=0
  constraints (38):
    c: Coincident(g-3,g0)
    c: Coincident(g0,g-3)
    c: Coincident(g0,g1)
    c: Coincident(g1,g-4)
    c: Coincident(g1,g2)
    c: Coincident(g2,g-4)
    c: Coincident(g2,g3)
    c: Coincident(g3,g4)
    c: Horizontal(g4)
    c: Coincident(g4,g5)
    c: Vertical(g5)
    c: Coincident(g5,g6)
    c: Horizontal(g6)
    c: Coincident(g6,g7)
    c: PointOnObject(g7,g-1)
    c: Vertical(g7)
    c: Coincident(g7,g8)
    c: PointOnObject(g8,g-1)
    c: Coincident(g8,g9)
    c: Coincident(g9,g0)
    c: Vertical(g9)
    c: Vertical(g3)
    c: Coincident(g10,g11)
    c: Coincident(g11,g12)
    c: Coincident(g12,g13)
    c: Coincident(g13,g10)
    c: Horizontal(g10)
    c: Horizontal(g12)
    c: Vertical(g11)
    c: Vertical(g13)
    c: PointOnObject(g10,g-1)
    c: Vertical(g12,g2)
    c: DistanceY(g13,g13) = 12.5
    c: DistanceX(g10,g10) = 2
    c: DistanceY(g3,g3) = 2.2
    c: DistanceX(g0,g5) = 2.4
    c: DistanceX(g8,g8) = 3.2
    c: DistanceY(g5,g0) = 2
FEATURE [PartDesign::Pocket] Pocket011
  BaseFeature = -> Pocket010
  Direction = (0,0,1)
  Length = 4
  Length2 = 5
  Profile = -> Sketch013
  ReferenceAxis = -> Sketch013 [N_Axis]
  Refine = true
  Suppressed = false
  Type = 0
FEATURE [Sketcher::SketchObject] Sketch014
  ArcFitTolerance = 1e-06
  AttachmentSupport = -> [Pocket011]
  ExternalGeometry = -> [Pocket011]
  FullyConstrained = false
  MakeInternals = false
  MapMode = 5
  Placement = pos=(0,0,21) rot=(0,0,1;0rad)
  sketch-geometry (9):
    g0: LineSegment StartX=73.35 StartY=27.75 StartZ=0 EndX=73.35 EndY=0 EndZ=0
    g1: LineSegment StartX=73.35 StartY=0 StartZ=0 EndX=89.95 EndY=0 EndZ=0
    g2-g5: Circle [constr] x4 (B-spline internal-alignment scaffolding for g6; pole/knot coordinates omitted)
    g6: BSplineCurve PolesCount=4 KnotsCount=2 Degree=3 IsPeriodic=0
    g7: GeomPoint [constr] X=89.95 Y=0 Z=0
    g8: GeomPoint [constr] X=73.35 Y=27.75 Z=0
  constraints (14):
    c: Coincident(g-3,g0)
    c: Coincident(g0,g-3)
    c: Coincident(g0,g1)
    c: PointOnObject(g1,g-1)
    c: DistanceX(g1,g1) = 16.6
    c: Weight(g2) = 1
    c: Equal(g2,g3)
    c: Equal(g2,g4)
    c: Equal(g2,g5)
    c: InternalAlignment(g2-g5 -> g6) x4
    c: InternalAlignment(g7,g6)
    c: InternalAlignment(g8,g6)
    c: Coincident(g2,g1)
    c: Coincident(g5,g0)
FEATURE [PartDesign::Pocket] Pocket012
  BaseFeature = -> Pocket011
  Direction = (0,0,-1)
  Length = 3
  Length2 = 5
  Profile = -> Sketch014
  ReferenceAxis = -> Sketch014 [N_Axis]
  Refine = true
  Suppressed = false
  Type = 0
FEATURE [Sketcher::SketchObject] Sketch015
  ArcFitTolerance = 1e-06
  AttachmentSupport = -> [Pocket012]
  ExternalGeometry = -> [Pocket012]
  FullyConstrained = true
  MakeInternals = false
  MapMode = 5
  Placement = pos=(0,27.75,0) rot=(1,0,0;1.5708rad)
  sketch-geometry (7):
    g0: LineSegment StartX=24.2 StartY=6 StartZ=0 EndX=73.35 EndY=6 EndZ=0
    g1: LineSegment StartX=73.35 StartY=6 StartZ=0 EndX=73.35 EndY=15 EndZ=0
    g2: LineSegment StartX=73.35 StartY=15 StartZ=0 EndX=51 EndY=15 EndZ=0
    g3: LineSegment StartX=51 StartY=15 StartZ=0 EndX=48.45 EndY=16 EndZ=0
    g4: LineSegment StartX=48.45 StartY=16 StartZ=0 EndX=25 EndY=16 EndZ=0
    g5: LineSegment StartX=25 StartY=16 StartZ=0 EndX=24.2 EndY=16.4 EndZ=0
    g6: LineSegment StartX=24.2 StartY=16.4 StartZ=0 EndX=24.2 EndY=6 EndZ=0
  constraints (19):
    c: Coincident(g-3,g0)
    c: Coincident(g0,g-4)
    c: Coincident(g0,g1)
    c: PointOnObject(g1,g-4)
    c: Coincident(g1,g2)
    c: Horizontal(g2)
    c: Coincident(g2,g3)
    c: Coincident(g3,g4)
    c: Horizontal(g4)
    c: Coincident(g4,g5)
    c: PointOnObject(g5,g-3)
    c: Coincident(g5,g6)
    c: Coincident(g6,g0)
    c: DistanceY(g6,g6) = 10.4
    c: DistanceY(g4) = 16
    c: DistanceX(g5,g4) = 0.8
    c: DistanceX(g4,g4) = 23.45
    c: DistanceY(g2) = 15
    c: DistanceX(g2,g2) = 22.35
FEATURE [PartDesign::Pocket] Pocket013
  BaseFeature = -> Pocket012
  Direction = (0,1,-2e-16)
  Length = 0
  Length2 = 5
  Profile = -> Sketch015
  ReferenceAxis = -> Sketch015 [N_Axis]
  Refine = true
  Suppressed = false
  Type = 3
  UpToFace = -> Pocket012 [Face35]
FEATURE [Sketcher::SketchObject] Sketch016
  ArcFitTolerance = 1e-06
  AttachmentSupport = -> [XY_Plane002]
  FullyConstrained = false
  MakeInternals = false
  MapMode = 5
  sketch-geometry (36):
    g0: LineSegment [constr] StartX=23.3 StartY=22.3 StartZ=0 EndX=59.9 EndY=22.3 EndZ=0
    g1: LineSegment [constr] StartX=59.9 StartY=22.3 StartZ=0 EndX=59.9 EndY=10.55 EndZ=0
    g2: LineSegment [constr] StartX=59.9 StartY=10.55 StartZ=0 EndX=72.15 EndY=10.55 EndZ=0
    g3: LineSegment [constr] StartX=72.15 StartY=10.55 StartZ=0 EndX=72.15 EndY=0 EndZ=0
    g4: LineSegment [constr] StartX=72.15 StartY=0 StartZ=0 EndX=80.25 EndY=2e-16 EndZ=0
    g5: LineSegment [constr] StartX=83.75 StartY=0 StartZ=0 EndX=92 EndY=0 EndZ=0
    g6: ArcOfCircle [constr] CenterX=82 CenterY=0 CenterZ=0 NormalX=0 NormalY=0 NormalZ=1 AngleXU=0 Radius=1.75 StartAngle=0 EndAngle=3.14159
    g7: LineSegment [constr] StartX=0 StartY=6.35e-14 StartZ=0 EndX=5.5 EndY=0 EndZ=0
    g8: LineSegment [constr] StartX=5.5 StartY=0 StartZ=0 EndX=5.5 EndY=18 EndZ=0
    g9: LineSegment [constr] StartX=5.5 StartY=18 StartZ=0 EndX=11 EndY=18 EndZ=0
    g10: LineSegment [constr] StartX=11 StartY=0 StartZ=0 EndX=23.3 EndY=0 EndZ=0
    g11: LineSegment StartX=0.05 StartY=7.2 StartZ=0 EndX=0.75 EndY=22.55 EndZ=0
    g12: ArcOfCircle CenterX=518.425 CenterY=0 CenterZ=0 NormalX=0 NormalY=0 NormalZ=1 AngleXU=0 Radius=518.425 StartAngle=3.1277 EndAngle=3.14159
    g13: LineSegment [constr] StartX=11 StartY=0 StartZ=0 EndX=11 EndY=18 EndZ=0
    g14: LineSegment StartX=20.1 StartY=35.5 StartZ=0 EndX=64.2 EndY=35.5 EndZ=0
    g15-g20: Circle [constr] x6 (B-spline internal-alignment scaffolding for g21; pole/knot coordinates omitted)
    g21: BSplineCurve PolesCount=6 KnotsCount=4 Degree=3 IsPeriodic=0
    g22-g25: GeomPoint [constr] x4 (B-spline internal-alignment scaffolding for g21; pole/knot coordinates omitted)
    g26-g29: Circle [constr] x4 (B-spline internal-alignment scaffolding for g30; pole/knot coordinates omitted)
    g30: BSplineCurve PolesCount=4 KnotsCount=2 Degree=3 IsPeriodic=0
    g31: GeomPoint [constr] X=92 Y=0 Z=0
    g32: GeomPoint [constr] X=64.2 Y=35.5 Z=0
    g33: Circle [constr] CenterX=17 CenterY=25 CenterZ=0 NormalX=0 NormalY=0 NormalZ=1 AngleXU=0 Radius=1.75
    g34: LineSegment [constr] StartX=23.3 StartY=0 StartZ=0 EndX=23.3 EndY=22.3 EndZ=0
    g35: LineSegment StartX=0 StartY=6.35e-14 StartZ=0 EndX=92 EndY=0 EndZ=0
  constraints (73):
    c: PointOnObject(g10,g-1)
    c: Horizontal(g0)
    c: Coincident(g0,g1)
    c: Vertical(g1)
    c: Coincident(g1,g2)
    c: Horizontal(g2)
    c: Coincident(g2,g3)
    c: PointOnObject(g3,g-1)
    c: Vertical(g3)
    c: Coincident(g4,g3)
    c: PointOnObject(g4,g-1)
    c: PointOnObject(g5,g-1)
    c: PointOnObject(g5,g-1)
    c: Coincident(g6,g4)
    c: Coincident(g6,g5)
    c: PointOnObject(g6,g-1)
    c: Coincident(g7,g-1)
    c: PointOnObject(g7,g-1)
    c: Coincident(g8,g7)
    c: Vertical(g8)
    c: Horizontal(g9)
    c: PointOnObject(g10,g-1)
    c: DistanceX(g7,g7) = 5.5
    c: DistanceX(g7,g10) = 5.5
    c: Coincident(g9,g8)
    c: DistanceY(g8,g8) = 18
    c: Diameter(g6) = 3.5
    c: DistanceX(g5,g5) = 8.25
    c: DistanceX(g5) = 92
    c: DistanceX(g11) = 0.75
    c: DistanceY(g11) = 22.55
    c: Coincident(g12,g7)
    c: Coincident(g12,g11)
    c: DistanceX(g11) = 0.05
    c: DistanceY(g11) = 7.2
    c: Perpendicular(g12,g-1)
    c: Radius(g12) = 518.425
    c: Coincident(g13,g10)
    c: Coincident(g13,g9)
    c: Vertical(g13)
    c: Horizontal(g14)
    c: DistanceY(g14) = 35.5
    c: DistanceX(g14) = 20.1
    c: DistanceX(g14,g14) = 44.1
    c: Weight(g15) = 1
    c: Equal(g15, g16-g20) x5
    c: InternalAlignment(g15-g20 -> g21) x6
    c: InternalAlignment(g22-g25 -> g21) x4
    c: Coincident(g15,g11)
    c: Coincident(g20,g14)
    c: Weight(g26) = 1
    c: Equal(g26,g27)
    c: Equal(g26,g28)
    c: Equal(g26,g29)
    c: InternalAlignment(g26-g29 -> g30) x4
    c: InternalAlignment(g31,g30)
    c: InternalAlignment(g32,g30)
    c: Coincident(g26,g5)
    c: Coincident(g29,g14)
    c: DistanceY(g33) = 25
    c: DistanceX(g33,g6) = 65
    c: Equal(g33,g6)
    c: Coincident(g34,g10)
    c: Coincident(g34,g0)
    c: Vertical(g34)
    c: DistanceX(g10,g10) = 12.3
    c: DistanceY(g34,g34) = 22.3
    c: DistanceX(g0,g0) = 36.6
    c: DistanceY(g1,g1) = 11.75
    c: DistanceX(g2,g2) = 12.25
    c: DistanceX(g4,g4) = 8.1
    c: Coincident(g35,g7)
    c: Coincident(g35,g30)
FEATURE [PartDesign::Pad] Pad002
  Direction = (0,0,1)
  Length = 12
  Length2 = 10
  Profile = -> Sketch016
  ReferenceAxis = -> Sketch016 [N_Axis]
  Refine = true
  Suppressed = false
  Type = 0
FEATURE [Sketcher::SketchObject] Sketch017
  ArcFitTolerance = 1e-06
  AttachmentSupport = -> [Pad002]
  ExternalGeometry = -> [Pad002]
  FullyConstrained = true
  MakeInternals = false
  MapMode = 5
  Placement = pos=(0,0,12) rot=(0,0,1;0rad)
  sketch-geometry (36):
    g0: ArcOfCircle CenterX=82 CenterY=0 CenterZ=0 NormalX=0 NormalY=0 NormalZ=1 AngleXU=0 Radius=2.5 StartAngle=0 EndAngle=3.14159
    g1: Circle CenterX=17 CenterY=25 CenterZ=0 NormalX=0 NormalY=0 NormalZ=1 AngleXU=0 Radius=2.5
    g2: LineSegment StartX=2 StartY=0 StartZ=0 EndX=2.57586 EndY=18.6857 EndZ=0
    g3: ArcOfCircle CenterX=82 CenterY=0 CenterZ=0 NormalX=0 NormalY=0 NormalZ=1 AngleXU=0 Radius=6 StartAngle=1.5708 EndAngle=3.14159
    g4: ArcOfCircle CenterX=85.5 CenterY=8 CenterZ=0 NormalX=0 NormalY=0 NormalZ=1 AngleXU=0 Radius=2 StartAngle=4.71239 EndAngle=6.19002
    g5: ArcOfCircle CenterX=17 CenterY=25 CenterZ=0 NormalX=0 NormalY=0 NormalZ=1 AngleXU=0 Radius=6 StartAngle=3.14159 EndAngle=6.28319
    g6: ArcOfCircle CenterX=25 CenterY=31.5 CenterZ=0 NormalX=0 NormalY=0 NormalZ=1 AngleXU=0 Radius=2 StartAngle=1.5708 EndAngle=3.14159
    g7: ArcOfCircle CenterX=9 CenterY=28 CenterZ=0 NormalX=0 NormalY=0 NormalZ=1 AngleXU=0 Radius=2 StartAngle=2e-16 EndAngle=2.29046
    g8: ArcOfCircle CenterX=17.5687 CenterY=18.2237 CenterZ=0 NormalX=0 NormalY=0 NormalZ=1 AngleXU=0 Radius=15 StartAngle=2.29046 EndAngle=3.11078
    g9: LineSegment StartX=23 StartY=25 StartZ=0 EndX=23 EndY=31.5 EndZ=0
    g10: LineSegment StartX=11 StartY=25 StartZ=0 EndX=11 EndY=28 EndZ=0
    g11: LineSegment StartX=82 StartY=6 StartZ=0 EndX=85.5 EndY=6 EndZ=0
    g12: ArcOfCircle CenterX=64.0932 CenterY=10.0002 CenterZ=0 NormalX=0 NormalY=0 NormalZ=1 AngleXU=0 Radius=23.5 StartAngle=6.19002 EndAngle=7.84944
    g13: LineSegment StartX=79.5 StartY=0 StartZ=0 EndX=84.5 EndY=0 EndZ=0
    g14: LineSegment StartX=2 StartY=0 StartZ=0 EndX=16 EndY=0 EndZ=0
    g15: LineSegment StartX=16 StartY=0 StartZ=0 EndX=16 EndY=1 EndZ=0
    g16: LineSegment StartX=16 StartY=1 StartZ=0 EndX=22 EndY=1 EndZ=0
    g17: LineSegment StartX=22 StartY=1 StartZ=0 EndX=22 EndY=8e-16 EndZ=0
    g18: LineSegment StartX=22 StartY=8e-16 StartZ=0 EndX=76 EndY=8e-16 EndZ=0
    g19: ArcOfCircle CenterX=28 CenterY=31.5 CenterZ=0 NormalX=0 NormalY=0 NormalZ=1 AngleXU=0 Radius=2 StartAngle=2e-16 EndAngle=1.5708
    g20: ArcOfCircle CenterX=32 CenterY=12 CenterZ=0 NormalX=0 NormalY=0 NormalZ=1 AngleXU=0 Radius=2 StartAngle=3.14159 EndAngle=4.71239
    g21: ArcOfCircle CenterX=34 CenterY=12 CenterZ=0 NormalX=0 NormalY=0 NormalZ=1 AngleXU=0 Radius=2 StartAngle=4.71239 EndAngle=6.28319
    g22: ArcOfCircle CenterX=38 CenterY=31.5 CenterZ=0 NormalX=0 NormalY=0 NormalZ=1 AngleXU=0 Radius=2 StartAngle=1.5708 EndAngle=3.14159
    g23: ArcOfCircle CenterX=45.2 CenterY=31.5 CenterZ=0 NormalX=0 NormalY=0 NormalZ=1 AngleXU=0 Radius=2 StartAngle=4e-16 EndAngle=1.5708
    g24: ArcOfCircle CenterX=49.2 CenterY=12 CenterZ=0 NormalX=0 NormalY=0 NormalZ=1 AngleXU=0 Radius=2 StartAngle=3.14159 EndAngle=4.71239
    g25: ArcOfCircle CenterX=51.2 CenterY=12 CenterZ=0 NormalX=0 NormalY=0 NormalZ=1 AngleXU=0 Radius=2 StartAngle=4.71239 EndAngle=6.28319
    g26: ArcOfCircle CenterX=55.2 CenterY=31.5 CenterZ=0 NormalX=0 NormalY=0 NormalZ=1 AngleXU=0 Radius=2 StartAngle=1.5708 EndAngle=3.14159
    g27: LineSegment StartX=55.2 StartY=33.5 StartZ=0 EndX=64.2 EndY=33.5 EndZ=0
    g28: LineSegment StartX=53.2 StartY=31.5 StartZ=0 EndX=53.2 EndY=12 EndZ=0
    g29: LineSegment StartX=51.2 StartY=10 StartZ=0 EndX=49.2 EndY=10 EndZ=0
    g30: LineSegment StartX=47.2 StartY=12 StartZ=0 EndX=47.2 EndY=31.5 EndZ=0
    g31: LineSegment StartX=45.2 StartY=33.5 StartZ=0 EndX=38 EndY=33.5 EndZ=0
    g32: LineSegment StartX=36 StartY=31.5 StartZ=0 EndX=36 EndY=12 EndZ=0
    g33: LineSegment StartX=34 StartY=10 StartZ=0 EndX=32 EndY=10 EndZ=0
    g34: LineSegment StartX=30 StartY=12 StartZ=0 EndX=30 EndY=31.5 EndZ=0
    g35: LineSegment StartX=28 StartY=33.5 StartZ=0 EndX=25 EndY=33.5 EndZ=0
  constraints (96):
    c: PointOnObject(g0,g-1)
    c: PointOnObject(g0,g-1)
    c: PointOnObject(g0,g-1)
    c: PointOnObject(g2,g-1)
    c: DistanceX(g-1,g2) = 2
    c: Vertical(g12,g-3)
    c: DistanceY(g12,g-3) = 2
    c: Vertical(g10)
    c: Tangent(g11,g4) = -1.5708
    c: Tangent(g11,g3) = 1.5708
    c: Tangent(g9,g6) = 1.5708
    c: Tangent(g9,g5) = -1.5708
    c: Tangent(g10,g5) = 1.5708
    c: Tangent(g10,g7) = -1.5708
    c: Vertical(g9)
    c: Coincident(g5,g1)
    c: Coincident(g3,g0)
    c: Horizontal(g11)
    c: Tangent(g8,g7) = -1.5708
    c: Equal(g1,g0)
    c: Diameter(g0) = 5
    c: Tangent(g12,g4) = -1.5708
    c: Radius(g3) = 6
    c: Equal(g7,g6)
    c: Equal(g4,g6)
    c: Radius(g4) = 2
    c: Tangent(g8,g2) = 1.5708
    c: Equal(g3,g5)
    c: DistanceY(g1) = 25
    c: DistanceX(g1) = 17
    c: DistanceX(g1,g0) = 65
    c: Radius(g12) = 23.5
    c: Distance(g2,g-4) = 2
    c: Radius(g8) = 15
    c: DistanceY(g10,g10) = 3
    c: Coincident(g13,g0)
    c: Coincident(g13,g0)
    c: Coincident(g2,g14)
    c: PointOnObject(g14,g-1)
    c: Coincident(g14,g15)
    c: Coincident(g15,g16)
    c: Coincident(g16,g17)
    c: PointOnObject(g17,g-1)
    c: Vertical(g17)
    c: Coincident(g17,g18)
    c: Coincident(g18,g3)
    c: Horizontal(g18)
    c: DistanceX(g14) = 16
    c: Horizontal(g16)
    c: DistanceY(g15) = 1
    c: DistanceX(g16,g16) = 6
    c: Vertical(g15)
    c: Coincident(g27,g12)
    c: Horizontal(g31)
    c: Vertical(g32)
    c: Horizontal(g35)
    c: Tangent(g35,g6) = -1.5708
    c: Tangent(g35,g19) = -1.5708
    c: Tangent(g34,g19) = -1.5708
    c: Tangent(g34,g20) = 1.5708
    c: Tangent(g33,g20) = 1.5708
    c: Tangent(g33,g21) = 1.5708
    c: Tangent(g32,g21) = 1.5708
    c: Tangent(g32,g22) = -1.5708
    c: Tangent(g31,g22) = -1.5708
    c: Tangent(g31,g23) = -1.5708
    c: Tangent(g30,g23) = -1.5708
    c: Tangent(g30,g24) = 1.5708
    c: Tangent(g29,g24) = 1.5708
    c: Tangent(g29,g25) = 1.5708
    c: Tangent(g28,g25) = 1.5708
    c: Tangent(g27,g26) = 1.5708
    c: Tangent(g28,g26) = -1.5708
    c: Horizontal(g27)
    c: Vertical(g34)
    c: Horizontal(g33)
    c: Vertical(g30)
    c: Vertical(g28)
    c: Horizontal(g29)
    c: Horizontal(g23,g26)
    c: Horizontal(g24,g21)
    c: Equal(g25,g24)
    c: Equal(g24,g21)
    c: Equal(g21,g20)
    c: Horizontal(g19,g22)
    c: Equal(g19,g22)
    c: Equal(g22,g23)
    c: Equal(g23,g26)
    c: Equal(g6,g19)
    c: Equal(g19,g20)
    c: Equal(g33,g29)
    c: DistanceX(g35,g35) = 3
    c: DistanceX(g27,g27) = 9
    c: DistanceX(g33,g33) = 2
    c: DistanceY(g21) = 10
    c: DistanceX(g11,g11) = 3.5
FEATURE [TechDraw::DrawSVGTemplate] Template001
  EditableTexts = approval_person=B. Hecate; creator=Jon Sagebrand; date_of_issue=2026-02-18; document_type=Component Drawing; general_tolerances=ISO 2768-m; identification_number=DN; language_code=EN; legal_owner_1=Jonix; part_material=PETG; revision_index=AAA; scale=1 : 1; sheet_number=2 / 2; title=Makita LXT  - 18V - Battery holder
  Height = 210
  Orientation = 1
  Template = <path>
  Width = 297
FEATURE [TechDraw::DrawProjGroupItem] View001  label="Front"
  CoarseView = false
  Direction = (0,0,1)
  Focus = 100
  HardHidden = false
  IsoCount = 0
  IsoHidden = false
  IsoVisible = false
  LockPosition = true
  Perspective = false
  Rotation = 0
  RotationVector = (1,0,0)
  ScaleType = 2
  ScrubCount = 1
  SeamHidden = false
  SeamVisible = false
  SmoothHidden = false
  SmoothVisible = true
  Source = -> [Pocket013]
  Type = 0
  X = 0
  XDirection = (1,0,0)
  Y = 0
FEATURE [TechDraw::DrawProjGroupItem] ProjItem  label="Bottom"
  CoarseView = false
  Direction = (0,-1,0)
  Focus = 100
  HardHidden = false
  IsoCount = 0
  IsoHidden = false
  IsoVisible = false
  LockPosition = false
  Perspective = false
  Rotation = 0
  RotationVector = (1,0,0)
  ScaleType = 0
  ScrubCount = 1
  SeamHidden = false
  SeamVisible = false
  SmoothHidden = false
  SmoothVisible = true
  Source = -> [Pocket013]
  Type = 5
  X = 0
  XDirection = (1,0,0)
  Y = 43.25
FEATURE [TechDraw::DrawProjGroup] ProjGroup
  Anchor = -> View001
  AutoDistribute = true
  LockPosition = false
  ProjectionType = 0
  Rotation = 0
  ScaleType = 0
  Source = -> [Pocket013]
  Views = -> [View001,ProjItem]
  X = 148.5
  Y = 105
  spacingX = 15
  spacingY = 15
FEATURE [TechDraw::DrawViewDimension] Dimension006
  AngleOverride = false
  Arbitrary = false
  ArbitraryTolerances = false
  BoxCorners = (2) [(-46.0118,-17.75,-1e-07),(46.0118,17.75,1e-07)]
  EqualTolerance = true
  ExtensionAngle = 0
  FormatSpec = %.2w
  FormatSpecOverTolerance = %+.2w
  FormatSpecUnderTolerance = %+.2w
  Inverted = false
  LineAngle = 0
  LockPosition = false
  MeasureType = 1
  OverTolerance = 0
  References2D = -> [View001]
  Rotation = 0
  ScaleType = 0
  TheoreticalExact = false
  Type = 2
  UnderTolerance = 0
  X = -58.8145
  Y = -5.25
FEATURE [TechDraw::DrawViewDimension] Dimension007
  AngleOverride = false
  Arbitrary = false
  ArbitraryTolerances = false
  BoxCorners = (2) [(-46.0118,-17.75,-1e-07),(46.0118,17.75,1e-07)]
  EqualTolerance = true
  ExtensionAngle = 0
  FormatSpec = %.2w
  FormatSpecOverTolerance = %+.2w
  FormatSpecUnderTolerance = %+.2w
  Inverted = false
  LineAngle = 0
  LockPosition = false
  MeasureType = 1
  OverTolerance = 0
  References2D = -> [View001]
  Rotation = 0
  ScaleType = 0
  TheoreticalExact = false
  Type = 1
  UnderTolerance = 0
  X = -37.5118
  Y = -29.5131
FEATURE [TechDraw::DrawViewDimension] Dimension008
  AngleOverride = false
  Arbitrary = false
  ArbitraryTolerances = false
  BoxCorners = (2) [(-46.0118,-17.75,-1e-07),(46.0118,17.75,1e-07)]
  EqualTolerance = true
  ExtensionAngle = 0
  FormatSpec = %.2w
  FormatSpecOverTolerance = %+.2w
  FormatSpecUnderTolerance = %+.2w
  Inverted = false
  LineAngle = 0
  LockPosition = false
  MeasureType = 1
  OverTolerance = 0
  References2D = -> [View001]
  Rotation = 0
  ScaleType = 0
  TheoreticalExact = false
  Type = 1
  UnderTolerance = 0
  X = 3.48819
  Y = -29.5131
FEATURE [TechDraw::DrawPage] Page001
  KeepUpdated = true
  NextBalloonIndex = 1
  ProjectionType = 0
  Template = -> Template001
  Views = -> [ProjGroup,Dimension006,Dimension007,Dimension008]
FEATURE [PartDesign::Pocket] Pocket014
  BaseFeature = -> Pad002
  Direction = (0,0,-1)
  Length = 0
  Length2 = 5
  Offset = -2
  Profile = -> Sketch017
  ReferenceAxis = -> Sketch017 [N_Axis]
  Refine = true
  Suppressed = false
  Type = 3
  UpToFace = -> Pad002 [Face7]
FEATURE [Sketcher::SketchObject] Sketch018
  ArcFitTolerance = 1e-06
  AttachmentSupport = -> [Pocket014]
  ExternalGeometry = -> [Pocket014]
  FullyConstrained = true
  MakeInternals = false
  MapMode = 5
  Placement = pos=(0,6.35e-14,0) rot=(1,0,0;1.5708rad)
  sketch-geometry (5):
    g0: LineSegment StartX=22 StartY=12 StartZ=0 EndX=22 EndY=4 EndZ=0
    g1: LineSegment StartX=22 StartY=4 StartZ=0 EndX=18 EndY=10 EndZ=0
    g2: LineSegment StartX=18 StartY=10 StartZ=0 EndX=16 EndY=10 EndZ=0
    g3: LineSegment StartX=16 StartY=10 StartZ=0 EndX=16 EndY=12 EndZ=0
    g4: LineSegment StartX=16 StartY=12 StartZ=0 EndX=22 EndY=12 EndZ=0
  constraints (13):
    c: Vertical(g0)
    c: Coincident(g0,g1)
    c: Coincident(g1,g2)
    c: Horizontal(g2)
    c: Coincident(g2,g3)
    c: Coincident(g3,g-3)
    c: Vertical(g3)
    c: Coincident(g3,g4)
    c: Coincident(g4,g-3)
    c: Coincident(g0,g4)
    c: DistanceY(g-4,g0) = 2
    c: DistanceY(g-4,g1) = 8
    c: DistanceX(g2,g2) = 2
FEATURE [PartDesign::Pocket] Pocket015
  BaseFeature = -> Pocket014
  Direction = (0,1,-2e-16)
  Length = 5
  Length2 = 5
  Profile = -> Sketch018
  ReferenceAxis = -> Sketch018 [N_Axis]
  Refine = true
  Suppressed = false
  Type = 2
FEATURE [Sketcher::SketchObject] Sketch019
  ArcFitTolerance = 1e-06
  AttachmentSupport = -> [YZ_Plane002]
  FullyConstrained = true
  MakeInternals = false
  MapMode = 5
  Placement = pos=(0,0,0) rot=(0.57735,0.57735,0.57735;2.0944rad)
  sketch-geometry (4):
    g0: LineSegment StartX=0 StartY=2 StartZ=0 EndX=8 EndY=2 EndZ=0
    g1: LineSegment StartX=8 StartY=2 StartZ=0 EndX=8 EndY=10.3 EndZ=0
    g2: LineSegment StartX=8 StartY=10.3 StartZ=0 EndX=0 EndY=10.3 EndZ=0
    g3: LineSegment StartX=0 StartY=10.3 StartZ=0 EndX=0 EndY=2 EndZ=0
  constraints (12):
    c: Coincident(g0,g1)
    c: Coincident(g1,g2)
    c: Coincident(g2,g3)
    c: Coincident(g3,g0)
    c: Horizontal(g0)
    c: Horizontal(g2)
    c: Vertical(g1)
    c: Vertical(g3)
    c: PointOnObject(g0,g-2)
    c: DistanceX(g2,g2) = 8
    c: DistanceY(g3,g3) = 8.3
    c: DistanceY(g0) = 2
FEATURE [PartDesign::Pocket] Pocket016
  BaseFeature = -> Pocket015
  Direction = (-1,0,0)
  Length = 5
  Length2 = 5
  Profile = -> Sketch019
  ReferenceAxis = -> Sketch019 [N_Axis]
  Refine = true
  Reversed = true
  Suppressed = false
  Type = 0
FEATURE [Sketcher::SketchObject] Sketch020
  ArcFitTolerance = 1e-06
  AttachmentSupport = -> [Pocket013]
  ExternalGeometry = -> [Pocket013]
  FullyConstrained = true
  MakeInternals = false
  MapMode = 5
  Placement = pos=(0,0,18) rot=(0,0,1;0rad)
  sketch-geometry (2):
    g0: ArcOfCircle CenterX=82 CenterY=0 CenterZ=0 NormalX=0 NormalY=0 NormalZ=1 AngleXU=0 Radius=3 StartAngle=0 EndAngle=3.14159
    g1: LineSegment StartX=79 StartY=4e-16 StartZ=0 EndX=85 EndY=0 EndZ=0
  constraints (6):
    c: Coincident(g0,g-3)
    c: PointOnObject(g0,g-1)
    c: PointOnObject(g0,g-1)
    c: Diameter(g0) = 6
    c: Coincident(g1,g0)
    c: Coincident(g1,g0)
FEATURE [PartDesign::Pocket] Pocket017
  BaseFeature = -> Pocket013
  Direction = (0,0,-1)
  Length = 3
  Length2 = 5
  Profile = -> Sketch020
  ReferenceAxis = -> Sketch020 [N_Axis]
  Refine = true
  Suppressed = false
  Type = 0
FEATURE [Sketcher::SketchObject] Sketch021
  ArcFitTolerance = 1e-06
  AttachmentSupport = -> [Pocket017]
  ExternalGeometry = -> [Pocket017]
  FullyConstrained = true
  MakeInternals = false
  MapMode = 5
  Placement = pos=(0,0,6) rot=(0,0,1;0rad)
  sketch-geometry (1):
    g0: Circle CenterX=17 CenterY=25 CenterZ=0 NormalX=0 NormalY=0 NormalZ=1 AngleXU=0 Radius=3
  constraints (2):
    c: Coincident(g0,g-3)
    c: Diameter(g0) = 6
FEATURE [PartDesign::Pocket] Pocket018
  BaseFeature = -> Pocket017
  Direction = (0,0,-1)
  Length = 3
  Length2 = 5
  Profile = -> Sketch021
  ReferenceAxis = -> Sketch021 [N_Axis]
  Refine = true
  Suppressed = false
  Type = 0
FEATURE [PartDesign::Mirrored] Mirrored
  BaseFeature = -> Pocket018
  MirrorPlane = -> XZ_Plane001
  Originals = -> [Pocket018]
  Refine = true
  Suppressed = false
  TransformMode = 1
FEATURE [PartDesign::Body] Body001  label="Battery Mount v2"
  AllowCompound = false
  Group = -> [Sketch009,Pad001,Sketch010,Pocket008,Sketch011,Pocket009,Sketch012,Pocket010,Sketch013,Pocket011,Sketch014,Pocket012,Sketch015,Pocket013,Sketch020,Pocket017,Sketch021,Pocket018,Mirrored]
  Origin = -> Origin001
  Tip = -> Mirrored
FEATURE [Sketcher::SketchObject] Sketch022
  ArcFitTolerance = 1e-06
  AttachmentSupport = -> [Pocket016]
  ExternalGeometry = -> [Pocket016]
  FullyConstrained = true
  MakeInternals = false
  MapMode = 5
  Placement = pos=(0,0,12) rot=(0,0,1;0rad)
  sketch-geometry (16):
    g0: ArcOfCircle CenterX=34 CenterY=12 CenterZ=0 NormalX=0 NormalY=0 NormalZ=1 AngleXU=0 Radius=2 StartAngle=4.71239 EndAngle=6.28319
    g1: ArcOfCircle CenterX=32 CenterY=12 CenterZ=0 NormalX=0 NormalY=0 NormalZ=1 AngleXU=0 Radius=2 StartAngle=3.14159 EndAngle=4.71239
    g2: ArcOfCircle CenterX=49.2 CenterY=12 CenterZ=0 NormalX=0 NormalY=0 NormalZ=1 AngleXU=0 Radius=2 StartAngle=3.14159 EndAngle=4.71239
    g3: ArcOfCircle CenterX=51.2 CenterY=12 CenterZ=0 NormalX=0 NormalY=0 NormalZ=1 AngleXU=0 Radius=2 StartAngle=4.71239 EndAngle=6.28319
    g4: LineSegment StartX=32 StartY=10 StartZ=0 EndX=34 EndY=10 EndZ=0
    g5: LineSegment StartX=49.2 StartY=10 StartZ=0 EndX=51.2 EndY=10 EndZ=0
    g6: ArcOfCircle CenterX=32 CenterY=14 CenterZ=0 NormalX=0 NormalY=0 NormalZ=1 AngleXU=0 Radius=2 StartAngle=1.5708 EndAngle=3.14159
    g7: ArcOfCircle CenterX=34 CenterY=14 CenterZ=0 NormalX=0 NormalY=0 NormalZ=1 AngleXU=0 Radius=2 StartAngle=0 EndAngle=1.5708
    g8: ArcOfCircle CenterX=49.2 CenterY=14 CenterZ=0 NormalX=0 NormalY=0 NormalZ=1 AngleXU=0 Radius=2 StartAngle=1.5708 EndAngle=3.14159
    g9: ArcOfCircle CenterX=51.2 CenterY=14 CenterZ=0 NormalX=0 NormalY=0 NormalZ=1 AngleXU=0 Radius=2 StartAngle=2e-16 EndAngle=1.5708
    g10: LineSegment StartX=53.2 StartY=12 StartZ=0 EndX=53.2 EndY=14 EndZ=0
    g11: LineSegment StartX=47.2 StartY=12 StartZ=0 EndX=47.2 EndY=14 EndZ=0
    g12: LineSegment StartX=49.2 StartY=16 StartZ=0 EndX=51.2 EndY=16 EndZ=0
    g13: LineSegment StartX=36 StartY=12 StartZ=0 EndX=36 EndY=14 EndZ=0
    g14: LineSegment StartX=30 StartY=12 StartZ=0 EndX=30 EndY=14 EndZ=0
    g15: LineSegment StartX=32 StartY=16 StartZ=0 EndX=34 EndY=16 EndZ=0
  constraints (44):
    c: Coincident(g0,g-5)
    c: Coincident(g0,g-5)
    c: Coincident(g1,g-6)
    c: Coincident(g1,g-6)
    c: Coincident(g2,g-3)
    c: Coincident(g2,g-3)
    c: Coincident(g3,g-4)
    c: Coincident(g3,g-4)
    c: Coincident(g4,g1)
    c: Coincident(g4,g0)
    c: Coincident(g5,g2)
    c: Coincident(g5,g3)
    c: Equal(g3,g2)
    c: Equal(g2,g-3)
    c: Equal(g0,g1)
    c: Equal(g1,g-5)
    c: Coincident(g10,g3)
    c: Coincident(g11,g2)
    c: Coincident(g11,g8)
    c: Coincident(g12,g8)
    c: Coincident(g13,g0)
    c: Coincident(g14,g1)
    c: Coincident(g14,g6)
    c: Vertical(g14)
    c: Coincident(g15,g6)
    c: Vertical(g13)
    c: Vertical(g11)
    c: Vertical(g10)
    c: Horizontal(g12)
    c: Horizontal(g15)
    c: Equal(g14,g13)
    c: Equal(g13,g15)
    c: Equal(g15,g4)
    c: Equal(g4,g11)
    c: Equal(g11,g12)
    c: Equal(g12,g10)
    c: Equal(g3,g9)
    c: Equal(g9,g8)
    c: Equal(g8,g7)
    c: Equal(g7,g6)
    c: Tangent(g10,g9) = -1.5708
    c: Tangent(g12,g9) = 1.5708
    c: Tangent(g13,g7) = -1.5708
    c: Tangent(g15,g7) = 1.5708
FEATURE [PartDesign::Pad] Pad003
  BaseFeature = -> Pocket016
  Direction = (0,0,1)
  Length = 2.5
  Length2 = 10
  Profile = -> Sketch022
  ReferenceAxis = -> Sketch022 [N_Axis]
  Refine = true
  Suppressed = false
  Type = 0
FEATURE [Sketcher::SketchObject] Sketch023
  ArcFitTolerance = 1e-06
  AttachmentSupport = -> [XY_Plane003]
  FullyConstrained = false
  MakeInternals = false
  MapMode = 5
  sketch-geometry (74):
    g0: LineSegment [constr] StartX=23.3 StartY=57.8 StartZ=0 EndX=59.9 EndY=57.8 EndZ=0
    g1: LineSegment [constr] StartX=59.9 StartY=57.8 StartZ=0 EndX=59.9 EndY=46.05 EndZ=0
    g2: LineSegment [constr] StartX=59.9 StartY=46.05 StartZ=0 EndX=72.15 EndY=46.05 EndZ=0
    g3: LineSegment [constr] StartX=72.15 StartY=46.05 StartZ=0 EndX=72.15 EndY=35.5 EndZ=0
    g4: LineSegment [constr] StartX=72.15 StartY=35.5 StartZ=0 EndX=80.25 EndY=35.5 EndZ=0
    g5: LineSegment [constr] StartX=83.75 StartY=35.5 StartZ=0 EndX=92 EndY=35.5 EndZ=0
    g6: ArcOfCircle [constr] CenterX=82 CenterY=35.5 CenterZ=0 NormalX=0 NormalY=0 NormalZ=1 AngleXU=0 Radius=1.75 StartAngle=0 EndAngle=3.14159
    g7: LineSegment [constr] StartX=5.5 StartY=35.5 StartZ=0 EndX=5.5 EndY=53.5 EndZ=0
    g8: LineSegment [constr] StartX=5.5 StartY=53.5 StartZ=0 EndX=11 EndY=53.5 EndZ=0
    g9: LineSegment [constr] StartX=11 StartY=35.5 StartZ=0 EndX=23.3 EndY=35.5 EndZ=0
    g10: LineSegment StartX=0.05 StartY=42.7 StartZ=0 EndX=0.75 EndY=58.05 EndZ=0
    g11: LineSegment [constr] StartX=11 StartY=35.5 StartZ=0 EndX=11 EndY=53.5 EndZ=0
    g12: LineSegment StartX=20.1 StartY=71 StartZ=0 EndX=64.2 EndY=71 EndZ=0
    g13-g18: Circle [constr] x6 (B-spline internal-alignment scaffolding for g19; pole/knot coordinates omitted)
    g19: BSplineCurve PolesCount=6 KnotsCount=4 Degree=3 IsPeriodic=0
    g20-g23: GeomPoint [constr] x4 (B-spline internal-alignment scaffolding for g19; pole/knot coordinates omitted)
    g24-g27: Circle [constr] x4 (B-spline internal-alignment scaffolding for g28; pole/knot coordinates omitted)
    g28: BSplineCurve PolesCount=4 KnotsCount=2 Degree=3 IsPeriodic=0
    g29: GeomPoint [constr] X=92 Y=35.5 Z=0
    g30: GeomPoint [constr] X=64.2 Y=71 Z=0
    g31: Circle [constr] CenterX=17 CenterY=60.5 CenterZ=0 NormalX=0 NormalY=0 NormalZ=1 AngleXU=0 Radius=1.75
    g32: LineSegment [constr] StartX=23.3 StartY=35.5 StartZ=0 EndX=23.3 EndY=57.8 EndZ=0
    g33: LineSegment StartX=0.05 StartY=42.7 StartZ=0 EndX=0 EndY=35.5 EndZ=0
    g34: LineSegment [constr] StartX=0 StartY=35.5 StartZ=0 EndX=5.5 EndY=35.5 EndZ=0
    g35: LineSegment StartX=0 StartY=35.5 StartZ=0 EndX=0 EndY=0 EndZ=0
    g36: LineSegment StartX=92 StartY=35.5 StartZ=0 EndX=92 EndY=0 EndZ=0
    g37: LineSegment [constr] StartX=23.3 StartY=-57.8 StartZ=0 EndX=59.9 EndY=-57.8 EndZ=0
    g38: LineSegment [constr] StartX=59.9 StartY=-57.8 StartZ=0 EndX=59.9 EndY=-46.05 EndZ=0
    g39: LineSegment [constr] StartX=59.9 StartY=-46.05 StartZ=0 EndX=72.15 EndY=-46.05 EndZ=0
    g40: LineSegment [constr] StartX=72.15 StartY=-46.05 StartZ=0 EndX=72.15 EndY=-35.5 EndZ=0
    g41: LineSegment [constr] StartX=72.15 StartY=-35.5 StartZ=0 EndX=80.25 EndY=-35.5 EndZ=0
    g42: LineSegment [constr] StartX=83.75 StartY=-35.5 StartZ=0 EndX=92 EndY=-35.5 EndZ=0
    g43: ArcOfCircle [constr] CenterX=82 CenterY=-35.5 CenterZ=0 NormalX=0 NormalY=0 NormalZ=1 AngleXU=0 Radius=1.75 StartAngle=3.14159 EndAngle=6.28319
    g44: LineSegment [constr] StartX=5.5 StartY=-35.5 StartZ=0 EndX=5.5 EndY=-53.5 EndZ=0
    g45: LineSegment [constr] StartX=5.5 StartY=-53.5 StartZ=0 EndX=11 EndY=-53.5 EndZ=0
    g46: LineSegment [constr] StartX=11 StartY=-35.5 StartZ=0 EndX=23.3 EndY=-35.5 EndZ=0
    g47: LineSegment StartX=0.05 StartY=-42.7 StartZ=0 EndX=0.75 EndY=-58.05 EndZ=0
    g48: LineSegment [constr] StartX=11 StartY=-35.5 StartZ=0 EndX=11 EndY=-53.5 EndZ=0
    g49: LineSegment StartX=20.1 StartY=-71 StartZ=0 EndX=64.2 EndY=-71 EndZ=0
    g50-g55: Circle [constr] x6 (B-spline internal-alignment scaffolding for g56; pole/knot coordinates omitted)
    g56: BSplineCurve PolesCount=6 KnotsCount=4 Degree=3 IsPeriodic=0
    g57-g60: GeomPoint [constr] x4 (B-spline internal-alignment scaffolding for g56; pole/knot coordinates omitted)
    g61-g64: Circle [constr] x4 (B-spline internal-alignment scaffolding for g65; pole/knot coordinates omitted)
    g65: BSplineCurve PolesCount=4 KnotsCount=2 Degree=3 IsPeriodic=0
    g66: GeomPoint [constr] X=92 Y=-35.5 Z=0
    g67: GeomPoint [constr] X=64.2 Y=-71 Z=0
    g68: Circle [constr] CenterX=17 CenterY=-60.5 CenterZ=0 NormalX=0 NormalY=0 NormalZ=1 AngleXU=0 Radius=1.75
    g69: LineSegment [constr] StartX=23.3 StartY=-35.5 StartZ=0 EndX=23.3 EndY=-57.8 EndZ=0
    g70: LineSegment StartX=0.05 StartY=-42.7 StartZ=0 EndX=0 EndY=-35.5 EndZ=0
    g71: LineSegment [constr] StartX=0 StartY=-35.5 StartZ=0 EndX=5.5 EndY=-35.5 EndZ=0
    g72: LineSegment StartX=0 StartY=-35.5 StartZ=0 EndX=0 EndY=0 EndZ=0
    g73: LineSegment StartX=92 StartY=-35.5 StartZ=0 EndX=92 EndY=0 EndZ=0
  constraints (129):
    c: Horizontal(g0)
    c: Coincident(g0,g1)
    c: Vertical(g1)
    c: Coincident(g1,g2)
    c: Horizontal(g2)
    c: Coincident(g2,g3)
    c: Vertical(g3)
    c: Coincident(g4,g3)
    c: Coincident(g6,g4)
    c: Coincident(g6,g5)
    c: Vertical(g7)
    c: Horizontal(g8)
    c: DistanceX(g-1,g7) = 5.5
    c: DistanceX(g7,g9) = 5.5
    c: Coincident(g8,g7)
    c: Diameter(g6) = 3.5
    c: DistanceX(g5,g5) = 8.25
    c: DistanceX(g5) = 92
    c: DistanceX(g10) = 0.75
    c: DistanceX(g10) = 0.05
    c: Coincident(g11,g9)
    c: Coincident(g11,g8)
    c: Vertical(g11)
    c: Horizontal(g12)
    c: DistanceX(g12) = 20.1
    c: DistanceX(g12,g12) = 44.1
    c: Weight(g13) = 1
    c: Equal(g13, g14-g18) x5
    c: InternalAlignment(g13-g18 -> g19) x6
    c: InternalAlignment(g20-g23 -> g19) x4
    c: Coincident(g13,g10)
    c: Coincident(g18,g12)
    c: Weight(g24) = 1
    c: Equal(g24,g25)
    c: Equal(g24,g27)
    c: InternalAlignment(g24-g27 -> g28) x4
    c: InternalAlignment(g29,g28)
    c: InternalAlignment(g30,g28)
    c: Coincident(g24,g5)
    c: Coincident(g27,g12)
    c: DistanceX(g31,g6) = 65
    c: Equal(g31,g6)
    c: Coincident(g32,g9)
    c: Coincident(g32,g0)
    c: Vertical(g32)
    c: DistanceX(g9,g9) = 12.3
    c: DistanceY(g32,g32) = 22.3
    c: DistanceX(g0,g0) = 36.6
    c: DistanceY(g1,g1) = 11.75
    c: DistanceX(g2,g2) = 12.25
    c: DistanceX(g4,g4) = 8.1
    c: Horizontal(g7,g9)
    c: Horizontal(g9,g9)
    c: Horizontal(g9,g3)
    c: Horizontal(g3,g4)
    c: Horizontal(g4,g5)
    c: Horizontal(g5,g28)
    c: Coincident(g10,g33)
    c: Coincident(g33,g34)
    c: Coincident(g34,g7)
    c: PointOnObject(g33,g-2)
    c: Horizontal(g34)
    c: DistanceY(g7,g7) = 18
    c: DistanceY(g7,g10) = 7.2
    c: DistanceY(g7,g19) = 22.55
    c: DistanceY(g9,g31) = 25
    c: DistanceY(g9,g19) = 35.5
    c: DistanceX(g28,g25) = 0.39
    c: DistanceY(g28,g25) = 11.81
    c: DistanceY(g25,g26) = 23.27
    c: DistanceX(g26,g25) = 4.26
    c: DistanceY(g19,g14) = 1.96
    c: DistanceX(g19,g14) = 0.04043
    c: DistanceX(g14,g15) = 2.11
    c: DistanceY(g14,g15) = 3.83
    c: DistanceX(g15,g16) = 7.75
    c: DistanceY(g15,g16) = 6.89
    c: DistanceX(g16,g17) = 3.85
    c: DistanceY(g17,g16) = 0.41
    c: Horizontal(g4,g6)
    c: DistanceY(g33) = 35.5
    c: Coincident(g35,g33)
    c: Coincident(g35,g-1)
    c: Coincident(g36,g28)
    c: PointOnObject(g36,g-1)
    c: Vertical(g36)
    c: Horizontal(g37)
    c: Coincident(g37,g38)
    c: Vertical(g38)
    c: Coincident(g38,g39)
    c: Horizontal(g39)
    c: Coincident(g39,g40)
    c: Vertical(g40)
    c: Coincident(g41,g40)
    c: Coincident(g43,g41)
    c: Coincident(g43,g42)
    c: Vertical(g44)
    c: Horizontal(g45)
    c: Coincident(g45,g44)
    c: Diameter(g43) = 3.5
    c: Coincident(g48,g46)
    c: Coincident(g48,g45)
    c: Vertical(g48)
    c: Horizontal(g49)
    c: Weight(g50) = 1
    c: Equal(g50, g51-g55) x5
    c: InternalAlignment(g50-g55 -> g56) x6
    c: InternalAlignment(g57-g60 -> g56) x4
    c: Coincident(g50,g47)
    c: Coincident(g55,g49)
    c: Weight(g61) = 1
    c: Equal(g61,g62)
    c: Equal(g61,g64)
    c: InternalAlignment(g61-g64 -> g65) x4
    c: InternalAlignment(g66,g65)
    c: InternalAlignment(g67,g65)
    c: Coincident(g61,g42)
    c: Coincident(g64,g49)
    c: Equal(g68,g43)
    c: Coincident(g69,g46)
    c: Coincident(g69,g37)
    c: Vertical(g69)
    c: Coincident(g47,g70)
    c: Coincident(g70,g71)
    c: Coincident(g71,g44)
    c: Horizontal(g71)
    c: Coincident(g72,g70)
    c: Coincident(g73,g65)
    c: Vertical(g73)
FEATURE [PartDesign::Pad] Pad004
  Direction = (0,0,1)
  Length = 12
  Length2 = 10
  Profile = -> Sketch023
  ReferenceAxis = -> Sketch023 [N_Axis]
  Refine = true
  Suppressed = false
  Type = 0
FEATURE [PartDesign::Body] Body003  label="Double Bottom v2"
  AllowCompound = false
  Group = -> [Sketch023,Pad004]
  Origin = -> Origin003
  Tip = -> Pad004
FEATURE [PartDesign::Mirrored] Mirrored001
  BaseFeature = -> Pad003
  MirrorPlane = -> XZ_Plane002
  Originals = -> [Pad003]
  Refine = true
  Suppressed = false
  TransformMode = 1
FEATURE [PartDesign::Body] Body002  label="Single Bottom v2"
  AllowCompound = false
  Group = -> [Sketch016,Pad002,Sketch017,Pocket014,Sketch018,Pocket015,Sketch019,Pocket016,Sketch022,Pad003,Mirrored001]
  Origin = -> Origin002
  Placement = pos=(0,0,-12) rot=(0,0,1;0rad)
  Tip = -> Mirrored001
FEATURE [Sketcher::SketchObject] Sketch024
  ArcFitTolerance = 1e-06
  AttachmentSupport = -> [XY_Plane004]
  FullyConstrained = false
  MakeInternals = false
  MapMode = 5
  sketch-geometry (36):
    g0: LineSegment [constr] StartX=23.3 StartY=22.3 StartZ=0 EndX=59.9 EndY=22.3 EndZ=0
    g1: LineSegment [constr] StartX=59.9 StartY=22.3 StartZ=0 EndX=59.9 EndY=10.55 EndZ=0
    g2: LineSegment [constr] StartX=59.9 StartY=10.55 StartZ=0 EndX=72.15 EndY=10.55 EndZ=0
    g3: LineSegment [constr] StartX=72.15 StartY=10.55 StartZ=0 EndX=72.15 EndY=0 EndZ=0
    g4: LineSegment [constr] StartX=72.15 StartY=0 StartZ=0 EndX=80.25 EndY=2e-16 EndZ=0
    g5: LineSegment [constr] StartX=83.75 StartY=0 StartZ=0 EndX=92 EndY=0 EndZ=0
    g6: ArcOfCircle [constr] CenterX=82 CenterY=0 CenterZ=0 NormalX=0 NormalY=0 NormalZ=1 AngleXU=0 Radius=1.75 StartAngle=0 EndAngle=3.14159
    g7: LineSegment [constr] StartX=0 StartY=6.35e-14 StartZ=0 EndX=5.5 EndY=0 EndZ=0
    g8: LineSegment [constr] StartX=5.5 StartY=0 StartZ=0 EndX=5.5 EndY=18 EndZ=0
    g9: LineSegment [constr] StartX=5.5 StartY=18 StartZ=0 EndX=11 EndY=18 EndZ=0
    g10: LineSegment [constr] StartX=11 StartY=0 StartZ=0 EndX=23.3 EndY=0 EndZ=0
    g11: LineSegment StartX=0.05 StartY=7.2 StartZ=0 EndX=0.75 EndY=22.55 EndZ=0
    g12: ArcOfCircle CenterX=518.425 CenterY=0 CenterZ=0 NormalX=0 NormalY=0 NormalZ=1 AngleXU=0 Radius=518.425 StartAngle=3.1277 EndAngle=3.14159
    g13: LineSegment [constr] StartX=11 StartY=0 StartZ=0 EndX=11 EndY=18 EndZ=0
    g14: LineSegment StartX=20.1 StartY=35.5 StartZ=0 EndX=64.2 EndY=35.5 EndZ=0
    g15-g20: Circle [constr] x6 (B-spline internal-alignment scaffolding for g21; pole/knot coordinates omitted)
    g21: BSplineCurve PolesCount=6 KnotsCount=4 Degree=3 IsPeriodic=0
    g22-g25: GeomPoint [constr] x4 (B-spline internal-alignment scaffolding for g21; pole/knot coordinates omitted)
    g26-g29: Circle [constr] x4 (B-spline internal-alignment scaffolding for g30; pole/knot coordinates omitted)
    g30: BSplineCurve PolesCount=4 KnotsCount=2 Degree=3 IsPeriodic=0
    g31: GeomPoint [constr] X=92 Y=0 Z=0
    g32: GeomPoint [constr] X=64.2 Y=35.5 Z=0
    g33: Circle [constr] CenterX=17 CenterY=25 CenterZ=0 NormalX=0 NormalY=0 NormalZ=1 AngleXU=0 Radius=1.75
    g34: LineSegment [constr] StartX=23.3 StartY=0 StartZ=0 EndX=23.3 EndY=22.3 EndZ=0
    g35: LineSegment StartX=0 StartY=6.35e-14 StartZ=0 EndX=92 EndY=0 EndZ=0
  constraints (73):
    c: PointOnObject(g10,g-1)
    c: Horizontal(g0)
    c: Coincident(g0,g1)
    c: Vertical(g1)
    c: Coincident(g1,g2)
    c: Horizontal(g2)
    c: Coincident(g2,g3)
    c: PointOnObject(g3,g-1)
    c: Vertical(g3)
    c: Coincident(g4,g3)
    c: PointOnObject(g4,g-1)
    c: PointOnObject(g5,g-1)
    c: PointOnObject(g5,g-1)
    c: Coincident(g6,g4)
    c: Coincident(g6,g5)
    c: PointOnObject(g6,g-1)
    c: Coincident(g7,g-1)
    c: PointOnObject(g7,g-1)
    c: Coincident(g8,g7)
    c: Vertical(g8)
    c: Horizontal(g9)
    c: PointOnObject(g10,g-1)
    c: DistanceX(g7,g7) = 5.5
    c: DistanceX(g7,g10) = 5.5
    c: Coincident(g9,g8)
    c: DistanceY(g8,g8) = 18
    c: Diameter(g6) = 3.5
    c: DistanceX(g5,g5) = 8.25
    c: DistanceX(g5) = 92
    c: DistanceX(g11) = 0.75
    c: DistanceY(g11) = 22.55
    c: Coincident(g12,g7)
    c: Coincident(g12,g11)
    c: DistanceX(g11) = 0.05
    c: DistanceY(g11) = 7.2
    c: Perpendicular(g12,g-1)
    c: Radius(g12) = 518.425
    c: Coincident(g13,g10)
    c: Coincident(g13,g9)
    c: Vertical(g13)
    c: Horizontal(g14)
    c: DistanceY(g14) = 35.5
    c: DistanceX(g14) = 20.1
    c: DistanceX(g14,g14) = 44.1
    c: Weight(g15) = 1
    c: Equal(g15, g16-g20) x5
    c: InternalAlignment(g15-g20 -> g21) x6
    c: InternalAlignment(g22-g25 -> g21) x4
    c: Coincident(g15,g11)
    c: Coincident(g20,g14)
    c: Weight(g26) = 1
    c: Equal(g26,g27)
    c: Equal(g26,g28)
    c: Equal(g26,g29)
    c: InternalAlignment(g26-g29 -> g30) x4
    c: InternalAlignment(g31,g30)
    c: InternalAlignment(g32,g30)
    c: Coincident(g26,g5)
    c: Coincident(g29,g14)
    c: DistanceY(g33) = 25
    c: DistanceX(g33,g6) = 65
    c: Equal(g33,g6)
    c: Coincident(g34,g10)
    c: Coincident(g34,g0)
    c: Vertical(g34)
    c: DistanceX(g10,g10) = 12.3
    c: DistanceY(g34,g34) = 22.3
    c: DistanceX(g0,g0) = 36.6
    c: DistanceY(g1,g1) = 11.75
    c: DistanceX(g2,g2) = 12.25
    c: DistanceX(g4,g4) = 8.1
    c: Coincident(g35,g7)
    c: Coincident(g35,g30)
FEATURE [PartDesign::Pad] Pad005
  Direction = (0,0,1)
  Length = 12
  Length2 = 10
  Profile = -> Sketch024
  ReferenceAxis = -> Sketch024 [N_Axis]
  Refine = true
  Suppressed = false
  Type = 0
FEATURE [Sketcher::SketchObject] Sketch025
  ArcFitTolerance = 1e-06
  AttachmentSupport = -> [Pad005]
  ExternalGeometry = -> [Pad005]
  FullyConstrained = true
  MakeInternals = false
  MapMode = 5
  Placement = pos=(0,0,12) rot=(0,0,1;0rad)
  sketch-geometry (36):
    g0: ArcOfCircle CenterX=82 CenterY=0 CenterZ=0 NormalX=0 NormalY=0 NormalZ=1 AngleXU=0 Radius=2.5 StartAngle=0 EndAngle=3.14159
    g1: Circle CenterX=17 CenterY=25 CenterZ=0 NormalX=0 NormalY=0 NormalZ=1 AngleXU=0 Radius=2.5
    g2: LineSegment StartX=2 StartY=0 StartZ=0 EndX=2.57586 EndY=18.6857 EndZ=0
    g3: ArcOfCircle CenterX=82 CenterY=0 CenterZ=0 NormalX=0 NormalY=0 NormalZ=1 AngleXU=0 Radius=6 StartAngle=1.5708 EndAngle=3.14159
    g4: ArcOfCircle CenterX=85.5 CenterY=8 CenterZ=0 NormalX=0 NormalY=0 NormalZ=1 AngleXU=0 Radius=2 StartAngle=4.71239 EndAngle=6.19002
    g5: ArcOfCircle CenterX=17 CenterY=25 CenterZ=0 NormalX=0 NormalY=0 NormalZ=1 AngleXU=0 Radius=6 StartAngle=3.14159 EndAngle=6.28319
    g6: ArcOfCircle CenterX=25 CenterY=31.5 CenterZ=0 NormalX=0 NormalY=0 NormalZ=1 AngleXU=0 Radius=2 StartAngle=1.5708 EndAngle=3.14159
    g7: ArcOfCircle CenterX=9 CenterY=28 CenterZ=0 NormalX=0 NormalY=0 NormalZ=1 AngleXU=0 Radius=2 StartAngle=9e-16 EndAngle=2.29046
    g8: ArcOfCircle CenterX=17.5687 CenterY=18.2237 CenterZ=0 NormalX=0 NormalY=0 NormalZ=1 AngleXU=0 Radius=15 StartAngle=2.29046 EndAngle=3.11078
    g9: LineSegment StartX=23 StartY=25 StartZ=0 EndX=23 EndY=31.5 EndZ=0
    g10: LineSegment StartX=11 StartY=25 StartZ=0 EndX=11 EndY=28 EndZ=0
    g11: LineSegment StartX=82 StartY=6 StartZ=0 EndX=85.5 EndY=6 EndZ=0
    g12: ArcOfCircle CenterX=64.0932 CenterY=10.0002 CenterZ=0 NormalX=0 NormalY=0 NormalZ=1 AngleXU=0 Radius=23.5 StartAngle=6.19002 EndAngle=7.84944
    g13: LineSegment StartX=79.5 StartY=3e-16 StartZ=0 EndX=84.5 EndY=0 EndZ=0
    g14: LineSegment StartX=2 StartY=0 StartZ=0 EndX=16 EndY=0 EndZ=0
    g15: LineSegment StartX=16 StartY=0 StartZ=0 EndX=16 EndY=1 EndZ=0
    g16: LineSegment StartX=16 StartY=1 StartZ=0 EndX=22 EndY=1 EndZ=0
    g17: LineSegment StartX=22 StartY=1 StartZ=0 EndX=22 EndY=0 EndZ=0
    g18: LineSegment StartX=22 StartY=0 StartZ=0 EndX=76 EndY=0 EndZ=0
    g19: ArcOfCircle CenterX=25.1 CenterY=31.5 CenterZ=0 NormalX=0 NormalY=0 NormalZ=1 AngleXU=0 Radius=2 StartAngle=6e-16 EndAngle=1.5708
    g20: ArcOfCircle CenterX=29.1 CenterY=12 CenterZ=0 NormalX=0 NormalY=0 NormalZ=1 AngleXU=0 Radius=2 StartAngle=3.14159 EndAngle=4.71239
    g21: ArcOfCircle CenterX=31.1 CenterY=12 CenterZ=0 NormalX=0 NormalY=0 NormalZ=1 AngleXU=0 Radius=2 StartAngle=4.71239 EndAngle=6.28319
    g22: ArcOfCircle CenterX=35.1 CenterY=31.5 CenterZ=0 NormalX=0 NormalY=0 NormalZ=1 AngleXU=0 Radius=2 StartAngle=1.5708 EndAngle=3.14159
    g23: ArcOfCircle CenterX=49.3 CenterY=31.5 CenterZ=0 NormalX=0 NormalY=0 NormalZ=1 AngleXU=0 Radius=2 StartAngle=0 EndAngle=1.5708
    g24: ArcOfCircle CenterX=53.3 CenterY=12 CenterZ=0 NormalX=0 NormalY=0 NormalZ=1 AngleXU=0 Radius=2 StartAngle=3.14159 EndAngle=4.71239
    g25: ArcOfCircle CenterX=55.3 CenterY=12 CenterZ=0 NormalX=0 NormalY=0 NormalZ=1 AngleXU=0 Radius=2 StartAngle=4.71239 EndAngle=6.28319
    g26: ArcOfCircle CenterX=59.3 CenterY=31.5 CenterZ=0 NormalX=0 NormalY=0 NormalZ=1 AngleXU=0 Radius=2 StartAngle=1.5708 EndAngle=3.14159
    g27: LineSegment StartX=59.3 StartY=33.5 StartZ=0 EndX=64.2 EndY=33.5 EndZ=0
    g28: LineSegment StartX=57.3 StartY=31.5 StartZ=0 EndX=57.3 EndY=12 EndZ=0
    g29: LineSegment StartX=55.3 StartY=10 StartZ=0 EndX=53.3 EndY=10 EndZ=0
    g30: LineSegment StartX=51.3 StartY=12 StartZ=0 EndX=51.3 EndY=31.5 EndZ=0
    g31: LineSegment StartX=49.3 StartY=33.5 StartZ=0 EndX=35.1 EndY=33.5 EndZ=0
    g32: LineSegment StartX=33.1 StartY=31.5 StartZ=0 EndX=33.1 EndY=12 EndZ=0
    g33: LineSegment StartX=31.1 StartY=10 StartZ=0 EndX=29.1 EndY=10 EndZ=0
    g34: LineSegment StartX=27.1 StartY=12 StartZ=0 EndX=27.1 EndY=31.5 EndZ=0
    g35: LineSegment StartX=25.1 StartY=33.5 StartZ=0 EndX=25 EndY=33.5 EndZ=0
  constraints (97):
    c: PointOnObject(g0,g-1)
    c: PointOnObject(g0,g-1)
    c: PointOnObject(g0,g-1)
    c: PointOnObject(g2,g-1)
    c: DistanceX(g-1,g2) = 2
    c: Vertical(g12,g-3)
    c: DistanceY(g12,g-3) = 2
    c: Vertical(g10)
    c: Tangent(g11,g4) = -1.5708
    c: Tangent(g11,g3) = 1.5708
    c: Tangent(g9,g6) = 1.5708
    c: Tangent(g9,g5) = -1.5708
    c: Tangent(g10,g5) = 1.5708
    c: Tangent(g10,g7) = -1.5708
    c: Vertical(g9)
    c: Coincident(g5,g1)
    c: Coincident(g3,g0)
    c: Horizontal(g11)
    c: Tangent(g8,g7) = -1.5708
    c: Equal(g1,g0)
    c: Diameter(g0) = 5
    c: Tangent(g12,g4) = -1.5708
    c: Radius(g3) = 6
    c: Equal(g7,g6)
    c: Equal(g4,g6)
    c: Radius(g4) = 2
    c: Tangent(g8,g2) = 1.5708
    c: Equal(g3,g5)
    c: DistanceY(g1) = 25
    c: DistanceX(g1) = 17
    c: DistanceX(g1,g0) = 65
    c: Radius(g12) = 23.5
    c: Distance(g2,g-4) = 2
    c: Radius(g8) = 15
    c: DistanceY(g10,g10) = 3
    c: Coincident(g13,g0)
    c: Coincident(g13,g0)
    c: Coincident(g2,g14)
    c: PointOnObject(g14,g-1)
    c: Coincident(g14,g15)
    c: Coincident(g15,g16)
    c: Coincident(g16,g17)
    c: PointOnObject(g17,g-1)
    c: Vertical(g17)
    c: Coincident(g17,g18)
    c: Coincident(g18,g3)
    c: Horizontal(g18)
    c: DistanceX(g14) = 16
    c: Horizontal(g16)
    c: DistanceY(g15) = 1
    c: DistanceX(g16,g16) = 6
    c: Vertical(g15)
    c: Coincident(g27,g12)
    c: Horizontal(g31)
    c: Vertical(g32)
    c: Horizontal(g35)
    c: Tangent(g35,g6) = -1.5708
    c: Tangent(g35,g19) = -1.5708
    c: Tangent(g34,g19) = -1.5708
    c: Tangent(g34,g20) = 1.5708
    c: Tangent(g33,g20) = 1.5708
    c: Tangent(g33,g21) = 1.5708
    c: Tangent(g32,g21) = 1.5708
    c: Tangent(g32,g22) = -1.5708
    c: Tangent(g31,g22) = -1.5708
    c: Tangent(g31,g23) = -1.5708
    c: Tangent(g30,g23) = -1.5708
    c: Tangent(g30,g24) = 1.5708
    c: Tangent(g29,g24) = 1.5708
    c: Tangent(g29,g25) = 1.5708
    c: Tangent(g28,g25) = 1.5708
    c: Tangent(g27,g26) = 1.5708
    c: Tangent(g28,g26) = -1.5708
    c: Horizontal(g27)
    c: Vertical(g34)
    c: Horizontal(g33)
    c: Vertical(g30)
    c: Vertical(g28)
    c: Horizontal(g29)
    c: Horizontal(g23,g26)
    c: Horizontal(g24,g21)
    c: Equal(g25,g24)
    c: Equal(g24,g21)
    c: Equal(g21,g20)
    c: Horizontal(g19,g22)
    c: Equal(g19,g22)
    c: Equal(g22,g23)
    c: Equal(g23,g26)
    c: Equal(g6,g19)
    c: Equal(g19,g20)
    c: Equal(g33,g29)
    c: DistanceX(g35,g35) = 0.1
    c: DistanceX(g27,g27) = 4.9
    c: DistanceX(g33,g33) = 2
    c: DistanceY(g21) = 10
    c: DistanceX(g11,g11) = 3.5
    c: DistanceX(g21,g24) = 18.2
FEATURE [PartDesign::Pocket] Pocket019
  BaseFeature = -> Pad005
  Direction = (0,0,-1)
  Length = 0
  Length2 = 5
  Offset = -2
  Profile = -> Sketch025
  ReferenceAxis = -> Sketch025 [N_Axis]
  Refine = true
  Suppressed = false
  Type = 3
  UpToFace = -> Pad005 [Face7]
FEATURE [Sketcher::SketchObject] Sketch026
  ArcFitTolerance = 1e-06
  AttachmentSupport = -> [Pocket019]
  ExternalGeometry = -> [Pocket019]
  FullyConstrained = true
  MakeInternals = false
  MapMode = 5
  Placement = pos=(0,6.35e-14,0) rot=(1,0,0;1.5708rad)
  sketch-geometry (5):
    g0: LineSegment StartX=22 StartY=12 StartZ=0 EndX=22 EndY=4 EndZ=0
    g1: LineSegment StartX=22 StartY=4 StartZ=0 EndX=18 EndY=10 EndZ=0
    g2: LineSegment StartX=18 StartY=10 StartZ=0 EndX=16 EndY=10 EndZ=0
    g3: LineSegment StartX=16 StartY=10 StartZ=0 EndX=16 EndY=12 EndZ=0
    g4: LineSegment StartX=16 StartY=12 StartZ=0 EndX=22 EndY=12 EndZ=0
  constraints (13):
    c: Vertical(g0)
    c: Coincident(g0,g1)
    c: Coincident(g1,g2)
    c: Horizontal(g2)
    c: Coincident(g2,g3)
    c: Coincident(g3,g-3)
    c: Vertical(g3)
    c: Coincident(g3,g4)
    c: Coincident(g4,g-3)
    c: Coincident(g0,g4)
    c: DistanceY(g-4,g0) = 2
    c: DistanceY(g-4,g1) = 8
    c: DistanceX(g2,g2) = 2
FEATURE [PartDesign::Pocket] Pocket020
  BaseFeature = -> Pocket019
  Direction = (0,1,-2e-16)
  Length = 5
  Length2 = 5
  Profile = -> Sketch026
  ReferenceAxis = -> Sketch026 [N_Axis]
  Refine = true
  Suppressed = false
  Type = 2
FEATURE [Sketcher::SketchObject] Sketch027
  ArcFitTolerance = 1e-06
  AttachmentSupport = -> [YZ_Plane004]
  FullyConstrained = true
  MakeInternals = false
  MapMode = 5
  Placement = pos=(0,0,0) rot=(0.57735,0.57735,0.57735;2.0944rad)
  sketch-geometry (4):
    g0: LineSegment StartX=0 StartY=2 StartZ=0 EndX=8 EndY=2 EndZ=0
    g1: LineSegment StartX=8 StartY=2 StartZ=0 EndX=8 EndY=10.3 EndZ=0
    g2: LineSegment StartX=8 StartY=10.3 StartZ=0 EndX=0 EndY=10.3 EndZ=0
    g3: LineSegment StartX=0 StartY=10.3 StartZ=0 EndX=0 EndY=2 EndZ=0
  constraints (12):
    c: Coincident(g0,g1)
    c: Coincident(g1,g2)
    c: Coincident(g2,g3)
    c: Coincident(g3,g0)
    c: Horizontal(g0)
    c: Horizontal(g2)
    c: Vertical(g1)
    c: Vertical(g3)
    c: PointOnObject(g0,g-2)
    c: DistanceX(g2,g2) = 8
    c: DistanceY(g3,g3) = 8.3
    c: DistanceY(g0) = 2
FEATURE [PartDesign::Pocket] Pocket021
  BaseFeature = -> Pocket020
  Direction = (-1,0,0)
  Length = 5
  Length2 = 5
  Profile = -> Sketch027
  ReferenceAxis = -> Sketch027 [N_Axis]
  Refine = true
  Reversed = true
  Suppressed = false
  Type = 0
FEATURE [Sketcher::SketchObject] Sketch028
  ArcFitTolerance = 1e-06
  AttachmentSupport = -> [Pocket021]
  ExternalGeometry = -> [Pocket021]
  FullyConstrained = true
  MakeInternals = false
  MapMode = 5
  Placement = pos=(0,0,12) rot=(0,0,1;0rad)
  sketch-geometry (16):
    g0: ArcOfCircle CenterX=31.1 CenterY=12 CenterZ=0 NormalX=0 NormalY=0 NormalZ=1 AngleXU=0 Radius=2 StartAngle=4.71239 EndAngle=6.28319
    g1: ArcOfCircle CenterX=29.1 CenterY=12 CenterZ=0 NormalX=0 NormalY=0 NormalZ=1 AngleXU=0 Radius=2 StartAngle=3.14159 EndAngle=4.71239
    g2: ArcOfCircle CenterX=53.3 CenterY=12 CenterZ=0 NormalX=0 NormalY=0 NormalZ=1 AngleXU=0 Radius=2 StartAngle=3.14159 EndAngle=4.71239
    g3: ArcOfCircle CenterX=55.3 CenterY=12 CenterZ=0 NormalX=0 NormalY=0 NormalZ=1 AngleXU=0 Radius=2 StartAngle=4.71239 EndAngle=6.28319
    g4: LineSegment StartX=29.1 StartY=10 StartZ=0 EndX=31.1 EndY=10 EndZ=0
    g5: LineSegment StartX=53.3 StartY=10 StartZ=0 EndX=55.3 EndY=10 EndZ=0
    g6: ArcOfCircle CenterX=29.1 CenterY=14 CenterZ=0 NormalX=0 NormalY=0 NormalZ=1 AngleXU=0 Radius=2 StartAngle=1.5708 EndAngle=3.14159
    g7: ArcOfCircle CenterX=31.1 CenterY=14 CenterZ=0 NormalX=0 NormalY=0 NormalZ=1 AngleXU=0 Radius=2 StartAngle=3e-16 EndAngle=1.5708
    g8: ArcOfCircle CenterX=53.3 CenterY=14 CenterZ=0 NormalX=0 NormalY=0 NormalZ=1 AngleXU=0 Radius=2 StartAngle=1.5708 EndAngle=3.14159
    g9: ArcOfCircle CenterX=55.3 CenterY=14 CenterZ=0 NormalX=0 NormalY=0 NormalZ=1 AngleXU=0 Radius=2 StartAngle=1e-16 EndAngle=1.5708
    g10: LineSegment StartX=57.3 StartY=12 StartZ=0 EndX=57.3 EndY=14 EndZ=0
    g11: LineSegment StartX=51.3 StartY=12 StartZ=0 EndX=51.3 EndY=14 EndZ=0
    g12: LineSegment StartX=53.3 StartY=16 StartZ=0 EndX=55.3 EndY=16 EndZ=0
    g13: LineSegment StartX=33.1 StartY=12 StartZ=0 EndX=33.1 EndY=14 EndZ=0
    g14: LineSegment StartX=27.1 StartY=12 StartZ=0 EndX=27.1 EndY=14 EndZ=0
    g15: LineSegment StartX=29.1 StartY=16 StartZ=0 EndX=31.1 EndY=16 EndZ=0
  constraints (44):
    c: Coincident(g0,g-5)
    c: Coincident(g0,g-5)
    c: Coincident(g1,g-6)
    c: Coincident(g1,g-6)
    c: Coincident(g2,g-3)
    c: Coincident(g2,g-3)
    c: Coincident(g3,g-4)
    c: Coincident(g3,g-4)
    c: Coincident(g4,g1)
    c: Coincident(g4,g0)
    c: Coincident(g5,g2)
    c: Coincident(g5,g3)
    c: Equal(g3,g2)
    c: Equal(g2,g-3)
    c: Equal(g0,g1)
    c: Equal(g1,g-5)
    c: Coincident(g10,g3)
    c: Coincident(g11,g2)
    c: Coincident(g11,g8)
    c: Coincident(g12,g8)
    c: Coincident(g13,g0)
    c: Coincident(g14,g1)
    c: Coincident(g14,g6)
    c: Vertical(g14)
    c: Coincident(g15,g6)
    c: Vertical(g13)
    c: Vertical(g11)
    c: Vertical(g10)
    c: Horizontal(g12)
    c: Horizontal(g15)
    c: Equal(g14,g13)
    c: Equal(g13,g15)
    c: Equal(g15,g4)
    c: Equal(g4,g11)
    c: Equal(g11,g12)
    c: Equal(g12,g10)
    c: Equal(g3,g9)
    c: Equal(g9,g8)
    c: Equal(g8,g7)
    c: Equal(g7,g6)
    c: Tangent(g10,g9) = -1.5708
    c: Tangent(g12,g9) = 1.5708
    c: Tangent(g13,g7) = -1.5708
    c: Tangent(g15,g7) = 1.5708
FEATURE [PartDesign::Pad] Pad006
  BaseFeature = -> Pocket021
  Direction = (0,0,1)
  Length = 3.5
  Length2 = 10
  Profile = -> Sketch028
  ReferenceAxis = -> Sketch028 [N_Axis]
  Refine = true
  Suppressed = false
  Type = 0
FEATURE [PartDesign::Mirrored] Mirrored002
  BaseFeature = -> Pad006
  MirrorPlane = -> XZ_Plane004
  Originals = -> [Pad006]
  Refine = true
  Suppressed = false
  TransformMode = 1
FEATURE [Sketcher::SketchObject] Sketch029
  ArcFitTolerance = 1e-06
  AttachmentSupport = -> [Mirrored002]
  ExternalGeometry = -> [Mirrored002]
  FullyConstrained = true
  MakeInternals = false
  MapMode = 5
  Placement = pos=(0,35.5,0) rot=(0,0.707107,0.707107;3.14159rad)
  sketch-geometry (6):
    g0: LineSegment StartX=-48.9 StartY=9.5 StartZ=0 EndX=-48.9 EndY=4.5 EndZ=0
    g1: LineSegment StartX=-48.9 StartY=4.5 StartZ=0 EndX=-36.4 EndY=4.5 EndZ=0
    g2: LineSegment StartX=-36.4 StartY=4.5 StartZ=0 EndX=-36.4 EndY=9.5 EndZ=0
    g3: LineSegment StartX=-36.4 StartY=9.5 StartZ=0 EndX=-48.9 EndY=9.5 EndZ=0
    g4: GeomPoint [constr] X=-42.65 Y=7 Z=0
    g5: LineSegment [constr] StartX=-51.3 StartY=7 StartZ=0 EndX=-34 EndY=7 EndZ=0
  constraints (16):
    c: Coincident(g0,g1)
    c: Coincident(g1,g2)
    c: Coincident(g2,g3)
    c: Coincident(g3,g0)
    c: Vertical(g0)
    c: Vertical(g2)
    c: Horizontal(g1)
    c: Horizontal(g3)
    c: Symmetric(g2,g0,g4)
    c: PointOnObject(g5,g-4)
    c: PointOnObject(g5,g-5)
    c: Horizontal(g5)
    c: Symmetric(g5,g5,g4)
    c: DistanceX(g3,g3) = 12.5
    c: DistanceY(g-3,g1) = 2.5
    c: DistanceY(g0,g0) = 5
FEATURE [PartDesign::Pocket] Pocket022
  BaseFeature = -> Mirrored002
  Direction = (0,-1,2e-16)
  Length = 5
  Length2 = 5
  Profile = -> Sketch029
  ReferenceAxis = -> Sketch029 [N_Axis]
  Refine = true
  Suppressed = false
  Type = 2
FEATURE [PartDesign::Body] Body004  label="Single Bottom v2 USB"
  AllowCompound = false
  Group = -> [Sketch024,Pad005,Sketch025,Pocket019,Sketch026,Pocket020,Sketch027,Pocket021,Sketch028,Pad006,Mirrored002,Sketch029,Pocket022]
  Origin = -> Origin004
  Placement = pos=(0,0,-12) rot=(0,0,1;0rad)
  Tip = -> Pocket022
note: 2 file-system paths scrubbed to <path> (originals preserved in the JSON sidecar)
